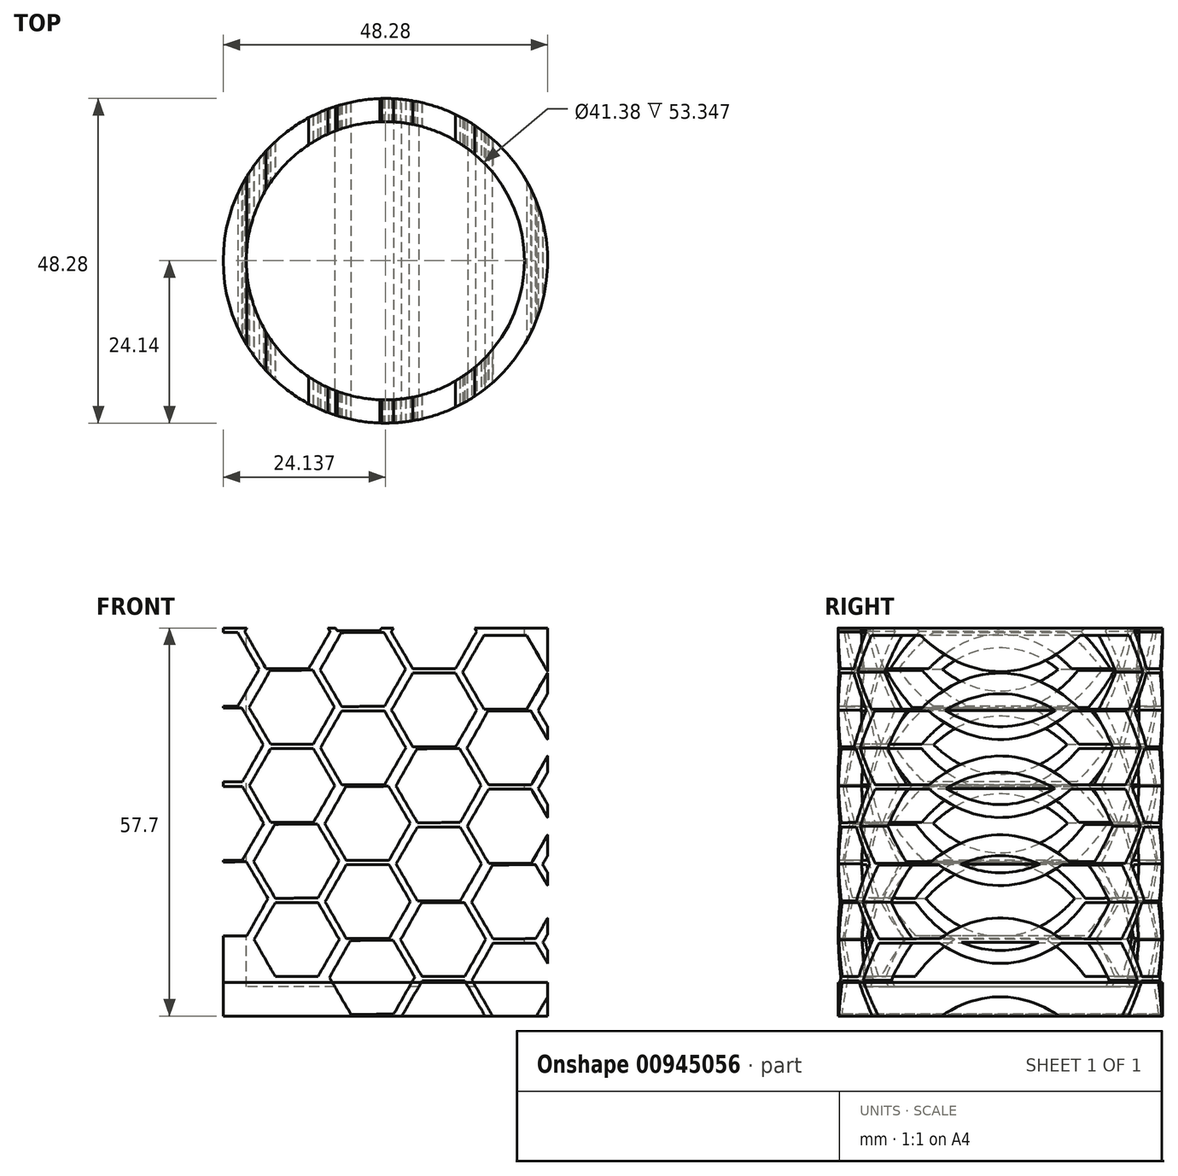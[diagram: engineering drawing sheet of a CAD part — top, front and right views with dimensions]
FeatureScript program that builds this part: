
annotation { "Feature Type Name" : "Feature", "Feature Type Description" : "" }
export const myFeature = defineFeature(function(context is Context, id is Id, definition is map)
    precondition{}
    {
        {
            var Q0;
            Q0=qCreatedBy(makeId("Front.planeOp"),FACE);
            var sketch = newSketch(context, id + "F0", { "sketchPlane" : qUnion([Q0])});
            skLineSegment(sketch, "E0", {"start": v(-46.54, 38.92) * mm, "end": v(-43.1, 38.92) * mm});
            skLineSegment(sketch, "E1", {"start": v(-46.54, 38.92) * mm, "end": v(-46.54, -18.78) * mm});
            skLineSegment(sketch, "E2", {"start": v(-43.1, 38.92) * mm, "end": v(-43.1, -14.43) * mm});
            skLineSegment(sketch, "E3", {"start": v(-43.1, -14.43) * mm, "end": v(-22.4, -14.43) * mm});
            skLineSegment(sketch, "E4", {"start": v(-22.4, -14.43) * mm, "end": v(-22.4, -18.78) * mm});
            skLineSegment(sketch, "E5", {"start": v(-22.4, -18.78) * mm, "end": v(-46.54, -18.78) * mm});
            skSolve(sketch);
        }
        {
            var Q0;
            Q0 = qSketchRegion(id + "F0", true);
            var Q1;
            Q1=sQuery(id+"F0.wireOp",EDGE,"E4");
            revolve(context, id + "F1", {"surfaceOperationType" : NewSurfaceOperationType.NEW, "entities" : qUnion([Q0]), "axis" : qUnion([Q1]), "revolveType" : RevolveType.FULL});
        }
        {
            var Q0;
            Q0=makeQuery(id+"F1.opRevolve","SWEPT_BODY",BODY,{"disambiguationData":[OSD([sQuery(id+"F0.wireOp",EDGE,"E0"),sQuery(id+"F0.wireOp",EDGE,"E1"),sQuery(id+"F0.wireOp",EDGE,"E2"),sQuery(id+"F0.wireOp",EDGE,"E3"),sQuery(id+"F0.wireOp",EDGE,"E4"),sQuery(id+"F0.wireOp",EDGE,"E5")])]});
            var Q1;
            Q1=qCreatedBy(makeId("Origin.pointOp"),VERTEX);
            transform(context, id + "F2", {"entities" : qUnion([Q0]), "transformType" : TransformType.TRANSLATION_3D, "dx" : 1 * mm, "dy" : 91.3 * mm, "dz" : -0.8 * mm, "makeCopy" : false});
        }
        {
            var Q0;
            Q0=qCreatedBy(makeId("Front.planeOp"),FACE);
            var sketch = newSketch(context, id + "F3", { "sketchPlane" : qUnion([Q0])});
            skCircle(sketch, "E6.cCircle", {"center": v(-88.91, 21.16) * mm, "radius": 5.5 * mm, "construction": true});
            skLineSegment(sketch, "E6.0", {"start": v(-82.56, 21.2) * mm, "end": v(-85.7, 15.69) * mm});
            skLineSegment(sketch, "E6.1", {"start": v(-85.7, 15.69) * mm, "end": v(-92.05, 15.64) * mm});
            skLineSegment(sketch, "E6.2", {"start": v(-92.05, 15.64) * mm, "end": v(-95.26, 21.12) * mm});
            skLineSegment(sketch, "E6.3", {"start": v(-95.26, 21.12) * mm, "end": v(-92.12, 26.64) * mm});
            skLineSegment(sketch, "E6.4", {"start": v(-92.12, 26.64) * mm, "end": v(-85.77, 26.69) * mm});
            skLineSegment(sketch, "E6.5", {"start": v(-85.77, 26.69) * mm, "end": v(-82.56, 21.2) * mm});
            skPoint(sketch, "E6.0.midPoint", {"position": v(-84.13, 18.45) * mm});
            skCircle(sketch, "E7.cCircle", {"center": v(-78.3, 15.13) * mm, "radius": 5.5 * mm, "construction": true});
            skLineSegment(sketch, "E7.0", {"start": v(-81.47, 9.63) * mm, "end": v(-84.65, 15.13) * mm});
            skLineSegment(sketch, "E7.1", {"start": v(-84.65, 15.13) * mm, "end": v(-81.47, 20.63) * mm});
            skLineSegment(sketch, "E7.2", {"start": v(-81.47, 20.63) * mm, "end": v(-75.12, 20.63) * mm});
            skLineSegment(sketch, "E7.3", {"start": v(-75.12, 20.63) * mm, "end": v(-71.94, 15.13) * mm});
            skLineSegment(sketch, "E7.4", {"start": v(-71.94, 15.13) * mm, "end": v(-75.12, 9.63) * mm});
            skLineSegment(sketch, "E7.5", {"start": v(-75.12, 9.63) * mm, "end": v(-81.47, 9.63) * mm});
            skPoint(sketch, "E7.0.midPoint", {"position": v(-83.06, 12.38) * mm});
            skLineSegment(sketch, "E8", {"start": v(-88.91, 21.16) * mm, "end": v(-78.3, 15.13) * mm});
            skLineSegment(sketch, "E9.1.0.0", {"start": v(-78.33, 26.78) * mm, "end": v(-67.72, 20.75) * mm});
            skLineSegment(sketch, "E9.1.0.1", {"start": v(-75.2, 32.3) * mm, "end": v(-71.98, 26.82) * mm});
            skPoint(sketch, "E9.1.0.2", {"position": v(-72.48, 18) * mm});
            skLineSegment(sketch, "E9.1.0.3", {"start": v(-81.47, 21.26) * mm, "end": v(-84.68, 26.74) * mm});
            skCircle(sketch, "E9.1.0.4", {"center": v(-67.72, 20.75) * mm, "radius": 5.5 * mm, "construction": true});
            skPoint(sketch, "E9.1.0.5", {"position": v(-73.55, 24.06) * mm});
            skCircle(sketch, "E9.1.0.6", {"center": v(-78.33, 26.78) * mm, "radius": 5.5 * mm, "construction": true});
            skLineSegment(sketch, "E9.1.0.7", {"start": v(-64.54, 15.25) * mm, "end": v(-70.9, 15.25) * mm});
            skLineSegment(sketch, "E9.1.0.8", {"start": v(-70.9, 15.25) * mm, "end": v(-74.07, 20.75) * mm});
            skLineSegment(sketch, "E9.1.0.9", {"start": v(-84.68, 26.74) * mm, "end": v(-81.55, 32.26) * mm});
            skLineSegment(sketch, "E9.1.0.10", {"start": v(-70.9, 26.25) * mm, "end": v(-64.54, 26.25) * mm});
            skLineSegment(sketch, "E9.1.0.11", {"start": v(-71.98, 26.82) * mm, "end": v(-75.12, 21.3) * mm});
            skLineSegment(sketch, "E9.1.0.12", {"start": v(-74.07, 20.75) * mm, "end": v(-70.9, 26.25) * mm});
            skLineSegment(sketch, "E9.1.0.13", {"start": v(-64.54, 26.25) * mm, "end": v(-61.37, 20.75) * mm});
            skLineSegment(sketch, "E9.1.0.14", {"start": v(-75.12, 21.3) * mm, "end": v(-81.47, 21.26) * mm});
            skLineSegment(sketch, "E9.1.0.15", {"start": v(-61.37, 20.75) * mm, "end": v(-64.54, 15.25) * mm});
            skLineSegment(sketch, "E9.1.0.16", {"start": v(-81.55, 32.26) * mm, "end": v(-75.2, 32.3) * mm});
            skLineSegment(sketch, "E9.2.0.0", {"start": v(-67.76, 32.4) * mm, "end": v(-57.14, 26.36) * mm});
            skLineSegment(sketch, "E9.2.0.1", {"start": v(-64.62, 37.92) * mm, "end": v(-61.4, 32.44) * mm});
            skPoint(sketch, "E9.2.0.2", {"position": v(-61.9, 23.61) * mm});
            skLineSegment(sketch, "E9.2.0.3", {"start": v(-70.9, 26.88) * mm, "end": v(-74.1, 32.35) * mm});
            skCircle(sketch, "E9.2.0.4", {"center": v(-57.14, 26.36) * mm, "radius": 5.5 * mm, "construction": true});
            skPoint(sketch, "E9.2.0.5", {"position": v(-62.97, 29.68) * mm});
            skCircle(sketch, "E9.2.0.6", {"center": v(-67.76, 32.4) * mm, "radius": 5.5 * mm, "construction": true});
            skLineSegment(sketch, "E9.2.0.7", {"start": v(-53.96, 20.86) * mm, "end": v(-60.31, 20.86) * mm});
            skLineSegment(sketch, "E9.2.0.8", {"start": v(-60.31, 20.86) * mm, "end": v(-63.5, 26.36) * mm});
            skLineSegment(sketch, "E9.2.0.9", {"start": v(-74.1, 32.35) * mm, "end": v(-70.97, 37.88) * mm});
            skLineSegment(sketch, "E9.2.0.10", {"start": v(-60.32, 31.86) * mm, "end": v(-53.96, 31.86) * mm});
            skLineSegment(sketch, "E9.2.0.11", {"start": v(-61.4, 32.44) * mm, "end": v(-64.54, 26.92) * mm});
            skLineSegment(sketch, "E9.2.0.12", {"start": v(-63.5, 26.36) * mm, "end": v(-60.32, 31.86) * mm});
            skLineSegment(sketch, "E9.2.0.13", {"start": v(-53.96, 31.86) * mm, "end": v(-50.79, 26.36) * mm});
            skLineSegment(sketch, "E9.2.0.14", {"start": v(-64.54, 26.92) * mm, "end": v(-70.9, 26.88) * mm});
            skLineSegment(sketch, "E9.2.0.15", {"start": v(-50.79, 26.36) * mm, "end": v(-53.96, 20.86) * mm});
            skLineSegment(sketch, "E9.2.0.16", {"start": v(-70.97, 37.88) * mm, "end": v(-64.62, 37.92) * mm});
            skLineSegment(sketch, "E9.3.0.0", {"start": v(-57.18, 38.01) * mm, "end": v(-46.56, 31.98) * mm});
            skLineSegment(sketch, "E9.3.0.1", {"start": v(-54.04, 43.54) * mm, "end": v(-50.83, 38.06) * mm});
            skPoint(sketch, "E9.3.0.2", {"position": v(-51.32, 29.23) * mm});
            skLineSegment(sketch, "E9.3.0.3", {"start": v(-60.32, 32.5) * mm, "end": v(-63.53, 37.97) * mm});
            skCircle(sketch, "E9.3.0.4", {"center": v(-46.56, 31.98) * mm, "radius": 5.5 * mm, "construction": true});
            skPoint(sketch, "E9.3.0.5", {"position": v(-52.4, 35.3) * mm});
            skCircle(sketch, "E9.3.0.6", {"center": v(-57.18, 38.01) * mm, "radius": 5.5 * mm, "construction": true});
            skLineSegment(sketch, "E9.3.0.7", {"start": v(-43.38, 26.48) * mm, "end": v(-49.74, 26.48) * mm});
            skLineSegment(sketch, "E9.3.0.8", {"start": v(-49.74, 26.48) * mm, "end": v(-52.91, 31.98) * mm});
            skLineSegment(sketch, "E9.3.0.9", {"start": v(-63.53, 37.97) * mm, "end": v(-60.4, 43.5) * mm});
            skLineSegment(sketch, "E9.3.0.10", {"start": v(-49.74, 37.48) * mm, "end": v(-43.39, 37.48) * mm});
            skLineSegment(sketch, "E9.3.0.11", {"start": v(-50.83, 38.06) * mm, "end": v(-53.97, 32.54) * mm});
            skLineSegment(sketch, "E9.3.0.12", {"start": v(-52.91, 31.98) * mm, "end": v(-49.74, 37.48) * mm});
            skLineSegment(sketch, "E9.3.0.13", {"start": v(-43.39, 37.48) * mm, "end": v(-40.21, 31.98) * mm});
            skLineSegment(sketch, "E9.3.0.14", {"start": v(-53.97, 32.54) * mm, "end": v(-60.32, 32.5) * mm});
            skLineSegment(sketch, "E9.3.0.15", {"start": v(-40.21, 31.98) * mm, "end": v(-43.38, 26.48) * mm});
            skLineSegment(sketch, "E9.3.0.16", {"start": v(-60.4, 43.5) * mm, "end": v(-54.04, 43.54) * mm});
            skLineSegment(sketch, "E9.4.0.0", {"start": v(-46.6, 43.63) * mm, "end": v(-35.98, 37.6) * mm});
            skLineSegment(sketch, "E9.4.0.1", {"start": v(-43.46, 49.15) * mm, "end": v(-40.25, 43.67) * mm});
            skPoint(sketch, "E9.4.0.2", {"position": v(-40.75, 34.85) * mm});
            skLineSegment(sketch, "E9.4.0.3", {"start": v(-49.74, 38.1) * mm, "end": v(-52.95, 43.59) * mm});
            skCircle(sketch, "E9.4.0.4", {"center": v(-35.98, 37.6) * mm, "radius": 5.5 * mm, "construction": true});
            skPoint(sketch, "E9.4.0.5", {"position": v(-41.82, 40.91) * mm});
            skCircle(sketch, "E9.4.0.6", {"center": v(-46.6, 43.63) * mm, "radius": 5.5 * mm, "construction": true});
            skLineSegment(sketch, "E9.4.0.7", {"start": v(-32.8, 32.1) * mm, "end": v(-39.16, 32.1) * mm});
            skLineSegment(sketch, "E9.4.0.8", {"start": v(-39.16, 32.1) * mm, "end": v(-42.33, 37.6) * mm});
            skLineSegment(sketch, "E9.4.0.9", {"start": v(-52.95, 43.59) * mm, "end": v(-49.81, 49.1) * mm});
            skLineSegment(sketch, "E9.4.0.10", {"start": v(-39.16, 43.1) * mm, "end": v(-32.8, 43.1) * mm});
            skLineSegment(sketch, "E9.4.0.11", {"start": v(-40.25, 43.67) * mm, "end": v(-43.39, 38.15) * mm});
            skLineSegment(sketch, "E9.4.0.12", {"start": v(-42.33, 37.6) * mm, "end": v(-39.16, 43.1) * mm});
            skLineSegment(sketch, "E9.4.0.13", {"start": v(-32.8, 43.1) * mm, "end": v(-29.63, 37.6) * mm});
            skLineSegment(sketch, "E9.4.0.14", {"start": v(-43.39, 38.15) * mm, "end": v(-49.74, 38.1) * mm});
            skLineSegment(sketch, "E9.4.0.15", {"start": v(-29.63, 37.6) * mm, "end": v(-32.8, 32.1) * mm});
            skLineSegment(sketch, "E9.4.0.16", {"start": v(-49.81, 49.1) * mm, "end": v(-43.46, 49.15) * mm});
            skLineSegment(sketch, "E9.5.0.0", {"start": v(-36.02, 49.25) * mm, "end": v(-25.4, 43.21) * mm});
            skLineSegment(sketch, "E9.5.0.1", {"start": v(-32.88, 54.77) * mm, "end": v(-29.67, 49.3) * mm});
            skPoint(sketch, "E9.5.0.2", {"position": v(-30.17, 40.46) * mm});
            skLineSegment(sketch, "E9.5.0.3", {"start": v(-39.16, 43.73) * mm, "end": v(-42.37, 49.2) * mm});
            skCircle(sketch, "E9.5.0.4", {"center": v(-25.4, 43.21) * mm, "radius": 5.5 * mm, "construction": true});
            skPoint(sketch, "E9.5.0.5", {"position": v(-31.24, 46.53) * mm});
            skCircle(sketch, "E9.5.0.6", {"center": v(-36.02, 49.25) * mm, "radius": 5.5 * mm, "construction": true});
            skLineSegment(sketch, "E9.5.0.7", {"start": v(-22.23, 37.71) * mm, "end": v(-28.58, 37.71) * mm});
            skLineSegment(sketch, "E9.5.0.8", {"start": v(-28.58, 37.71) * mm, "end": v(-31.76, 43.21) * mm});
            skLineSegment(sketch, "E9.5.0.9", {"start": v(-42.37, 49.2) * mm, "end": v(-39.23, 54.73) * mm});
            skLineSegment(sketch, "E9.5.0.10", {"start": v(-28.58, 48.71) * mm, "end": v(-22.23, 48.71) * mm});
            skLineSegment(sketch, "E9.5.0.11", {"start": v(-29.67, 49.3) * mm, "end": v(-32.8, 43.77) * mm});
            skLineSegment(sketch, "E9.5.0.12", {"start": v(-31.76, 43.21) * mm, "end": v(-28.58, 48.71) * mm});
            skLineSegment(sketch, "E9.5.0.13", {"start": v(-22.23, 48.71) * mm, "end": v(-19.05, 43.21) * mm});
            skLineSegment(sketch, "E9.5.0.14", {"start": v(-32.8, 43.77) * mm, "end": v(-39.16, 43.73) * mm});
            skLineSegment(sketch, "E9.5.0.15", {"start": v(-19.05, 43.21) * mm, "end": v(-22.23, 37.71) * mm});
            skLineSegment(sketch, "E9.5.0.16", {"start": v(-39.23, 54.73) * mm, "end": v(-32.88, 54.77) * mm});
            skLineSegment(sketch, "E9.direction1", {"start": v(-92.05, 15.64) * mm, "end": v(-81.47, 21.26) * mm, "construction": true});
            skLineSegment(sketch, "E10.1.0.0", {"start": v(-70.2, 3.98) * mm, "end": v(-59.63, 9.6) * mm, "construction": true});
            skPoint(sketch, "E10.1.0.1", {"position": v(-19.97, 29.25) * mm});
            skPoint(sketch, "E10.1.0.2", {"position": v(-41.13, 18.02) * mm});
            skLineSegment(sketch, "E10.1.0.3", {"start": v(-53.35, 20.64) * mm, "end": v(-50.14, 15.16) * mm});
            skCircle(sketch, "E10.1.0.4", {"center": v(-24.72, 20.32) * mm, "radius": 5.5 * mm, "construction": true});
            skPoint(sketch, "E10.1.0.5", {"position": v(-30.55, 23.63) * mm});
            skLineSegment(sketch, "E10.1.0.6", {"start": v(-38.55, 31.83) * mm, "end": v(-32.2, 31.87) * mm});
            skLineSegment(sketch, "E10.1.0.7", {"start": v(-24.76, 31.97) * mm, "end": v(-14.14, 25.93) * mm});
            skLineSegment(sketch, "E10.1.0.8", {"start": v(-14.18, 37.59) * mm, "end": v(-3.56, 31.55) * mm});
            skLineSegment(sketch, "E10.1.0.9", {"start": v(-67.07, 9.5) * mm, "end": v(-56.45, 3.47) * mm});
            skCircle(sketch, "E10.1.0.10", {"center": v(-56.45, 3.47) * mm, "radius": 5.5 * mm, "construction": true});
            skCircle(sketch, "E10.1.0.11", {"center": v(-24.76, 31.97) * mm, "radius": 5.5 * mm, "construction": true});
            skLineSegment(sketch, "E10.1.0.12", {"start": v(-27.9, 26.45) * mm, "end": v(-31.1, 31.93) * mm});
            skPoint(sketch, "E10.1.0.13", {"position": v(-51.7, 12.4) * mm});
            skCircle(sketch, "E10.1.0.14", {"center": v(-3.56, 31.55) * mm, "radius": 5.5 * mm, "construction": true});
            skLineSegment(sketch, "E10.1.0.15", {"start": v(-45.91, 20.74) * mm, "end": v(-35.3, 14.7) * mm});
            skPoint(sketch, "E10.1.0.16", {"position": v(-61.21, 0.72) * mm});
            skPoint(sketch, "E10.1.0.17", {"position": v(-29.48, 17.57) * mm});
            skCircle(sketch, "E10.1.0.18", {"center": v(-14.18, 37.59) * mm, "radius": 5.5 * mm, "construction": true});
            skPoint(sketch, "E10.1.0.19", {"position": v(-62.29, 6.78) * mm});
            skCircle(sketch, "E10.1.0.20", {"center": v(-35.33, 26.35) * mm, "radius": 5.5 * mm, "construction": true});
            skCircle(sketch, "E10.1.0.21", {"center": v(-45.87, 9.08) * mm, "radius": 5.5 * mm, "construction": true});
            skLineSegment(sketch, "E10.1.0.22", {"start": v(-35.33, 26.35) * mm, "end": v(-24.72, 20.32) * mm});
            skCircle(sketch, "E10.1.0.23", {"center": v(-14.14, 25.93) * mm, "radius": 5.5 * mm, "construction": true});
            skCircle(sketch, "E10.1.0.24", {"center": v(-35.3, 14.7) * mm, "radius": 5.5 * mm, "construction": true});
            skPoint(sketch, "E10.1.0.25", {"position": v(-40.06, 11.95) * mm});
            skPoint(sketch, "E10.1.0.26", {"position": v(-8.32, 28.8) * mm});
            skPoint(sketch, "E10.1.0.27", {"position": v(-50.64, 6.33) * mm});
            skLineSegment(sketch, "E10.1.0.28", {"start": v(-21.62, 37.49) * mm, "end": v(-18.4, 32.01) * mm});
            skCircle(sketch, "E10.1.0.29", {"center": v(-45.91, 20.74) * mm, "radius": 5.5 * mm, "construction": true});
            skPoint(sketch, "E10.1.0.30", {"position": v(-9.4, 34.87) * mm});
            skCircle(sketch, "E10.1.0.31", {"center": v(-56.5, 15.12) * mm, "radius": 5.5 * mm, "construction": true});
            skCircle(sketch, "E10.1.0.32", {"center": v(-67.07, 9.5) * mm, "radius": 5.5 * mm, "construction": true});
            skPoint(sketch, "E10.1.0.33", {"position": v(-18.9, 23.18) * mm});
            skLineSegment(sketch, "E10.1.0.34", {"start": v(-56.5, 15.12) * mm, "end": v(-45.87, 9.08) * mm});
            skLineSegment(sketch, "E10.1.0.35", {"start": v(-10.97, 31.44) * mm, "end": v(-7.79, 25.94) * mm});
            skLineSegment(sketch, "E10.1.0.36", {"start": v(-32.12, 20.2) * mm, "end": v(-28.94, 14.7) * mm});
            skLineSegment(sketch, "E10.1.0.37", {"start": v(-49.05, 14.58) * mm, "end": v(-42.7, 14.59) * mm});
            skLineSegment(sketch, "E10.1.0.38", {"start": v(-0.39, 26.05) * mm, "end": v(-6.74, 26.05) * mm});
            skLineSegment(sketch, "E10.1.0.39", {"start": v(-42.7, 3.59) * mm, "end": v(-49.05, 3.58) * mm});
            skLineSegment(sketch, "E10.1.0.40", {"start": v(-28.98, 26.4) * mm, "end": v(-32.12, 20.87) * mm});
            skLineSegment(sketch, "E10.1.0.41", {"start": v(-17.4, 43.06) * mm, "end": v(-11.04, 43.1) * mm});
            skLineSegment(sketch, "E10.1.0.42", {"start": v(-42.7, 15.26) * mm, "end": v(-49.05, 15.21) * mm});
            skLineSegment(sketch, "E10.1.0.43", {"start": v(-20.53, 37.54) * mm, "end": v(-17.4, 43.06) * mm});
            skLineSegment(sketch, "E10.1.0.44", {"start": v(-52.22, 9.08) * mm, "end": v(-49.05, 14.58) * mm});
            skLineSegment(sketch, "E10.1.0.45", {"start": v(-50.14, 15.16) * mm, "end": v(-53.28, 9.64) * mm});
            skLineSegment(sketch, "E10.1.0.46", {"start": v(-50.1, 3.47) * mm, "end": v(-53.28, -2.03) * mm});
            skLineSegment(sketch, "E10.1.0.47", {"start": v(-7.79, 25.94) * mm, "end": v(-10.96, 20.44) * mm});
            skLineSegment(sketch, "E10.1.0.48", {"start": v(-6.74, 26.05) * mm, "end": v(-9.91, 31.55) * mm});
            skLineSegment(sketch, "E10.1.0.49", {"start": v(-32.12, 9.2) * mm, "end": v(-38.47, 9.2) * mm});
            skLineSegment(sketch, "E10.1.0.50", {"start": v(-42.7, 14.59) * mm, "end": v(-39.52, 9.09) * mm});
            skLineSegment(sketch, "E10.1.0.51", {"start": v(-32.12, 20.87) * mm, "end": v(-38.47, 20.83) * mm});
            skLineSegment(sketch, "E10.1.0.52", {"start": v(-53.28, 9.64) * mm, "end": v(-59.63, 9.6) * mm});
            skLineSegment(sketch, "E10.1.0.53", {"start": v(-60.72, 9.55) * mm, "end": v(-63.86, 4.02) * mm});
            skLineSegment(sketch, "E10.1.0.54", {"start": v(-0.39, 37.05) * mm, "end": v(2.79, 31.55) * mm});
            skLineSegment(sketch, "E10.1.0.55", {"start": v(-20.5, 25.93) * mm, "end": v(-17.32, 31.43) * mm});
            skLineSegment(sketch, "E10.1.0.56", {"start": v(-27.9, 25.82) * mm, "end": v(-21.54, 25.82) * mm});
            skLineSegment(sketch, "E10.1.0.57", {"start": v(-38.47, 9.2) * mm, "end": v(-41.65, 14.7) * mm});
            skLineSegment(sketch, "E10.1.0.58", {"start": v(-17.31, 20.43) * mm, "end": v(-20.5, 25.93) * mm});
            skLineSegment(sketch, "E10.1.0.59", {"start": v(-38.47, 20.83) * mm, "end": v(-41.68, 26.3) * mm});
            skLineSegment(sketch, "E10.1.0.60", {"start": v(-41.65, 14.7) * mm, "end": v(-38.47, 20.2) * mm});
            skLineSegment(sketch, "E10.1.0.61", {"start": v(-59.63, 8.97) * mm, "end": v(-53.28, 8.97) * mm});
            skLineSegment(sketch, "E10.1.0.62", {"start": v(-18.37, 20.32) * mm, "end": v(-21.54, 14.82) * mm});
            skLineSegment(sketch, "E10.1.0.63", {"start": v(-49.12, 26.21) * mm, "end": v(-42.77, 26.26) * mm});
            skLineSegment(sketch, "E10.1.0.64", {"start": v(-31.1, 31.93) * mm, "end": v(-27.97, 37.45) * mm});
            skLineSegment(sketch, "E10.1.0.65", {"start": v(-9.91, 31.55) * mm, "end": v(-6.74, 37.05) * mm});
            skLineSegment(sketch, "E10.1.0.66", {"start": v(-62.8, 3.47) * mm, "end": v(-59.63, 8.97) * mm});
            skLineSegment(sketch, "E10.1.0.67", {"start": v(-11.04, 43.1) * mm, "end": v(-7.83, 37.63) * mm});
            skLineSegment(sketch, "E10.1.0.68", {"start": v(-52.26, 20.7) * mm, "end": v(-49.12, 26.21) * mm});
            skLineSegment(sketch, "E10.1.0.69", {"start": v(-59.63, 9.6) * mm, "end": v(-62.84, 15.08) * mm});
            skLineSegment(sketch, "E10.1.0.70", {"start": v(-32.2, 31.87) * mm, "end": v(-28.98, 26.4) * mm});
            skLineSegment(sketch, "E10.1.0.71", {"start": v(-39.52, 9.09) * mm, "end": v(-42.7, 3.59) * mm});
            skLineSegment(sketch, "E10.1.0.72", {"start": v(-59.63, -2.03) * mm, "end": v(-62.8, 3.47) * mm});
            skLineSegment(sketch, "E10.1.0.73", {"start": v(-31.07, 20.32) * mm, "end": v(-27.9, 25.82) * mm});
            skLineSegment(sketch, "E10.1.0.74", {"start": v(-17.32, 31.43) * mm, "end": v(-10.97, 31.44) * mm});
            skLineSegment(sketch, "E10.1.0.75", {"start": v(-21.54, 26.5) * mm, "end": v(-27.9, 26.45) * mm});
            skLineSegment(sketch, "E10.1.0.76", {"start": v(-59.7, 20.6) * mm, "end": v(-53.35, 20.64) * mm});
            skLineSegment(sketch, "E10.1.0.77", {"start": v(-62.84, 15.08) * mm, "end": v(-59.7, 20.6) * mm});
            skLineSegment(sketch, "E10.1.0.78", {"start": v(-27.97, 37.45) * mm, "end": v(-21.62, 37.49) * mm});
            skLineSegment(sketch, "E10.1.0.79", {"start": v(-39.56, 20.78) * mm, "end": v(-42.7, 15.26) * mm});
            skLineSegment(sketch, "E10.1.0.80", {"start": v(-73.42, 9.46) * mm, "end": v(-70.28, 14.98) * mm});
            skLineSegment(sketch, "E10.1.0.81", {"start": v(-17.32, 32.06) * mm, "end": v(-20.53, 37.54) * mm});
            skLineSegment(sketch, "E10.1.0.82", {"start": v(-63.93, 15.02) * mm, "end": v(-60.72, 9.55) * mm});
            skLineSegment(sketch, "E10.1.0.83", {"start": v(-42.77, 26.26) * mm, "end": v(-39.56, 20.78) * mm});
            skLineSegment(sketch, "E10.1.0.84", {"start": v(-38.47, 20.2) * mm, "end": v(-32.12, 20.2) * mm});
            skLineSegment(sketch, "E10.1.0.85", {"start": v(-41.68, 26.3) * mm, "end": v(-38.55, 31.83) * mm});
            skLineSegment(sketch, "E10.1.0.86", {"start": v(-21.54, 14.82) * mm, "end": v(-27.9, 14.82) * mm});
            skLineSegment(sketch, "E10.1.0.87", {"start": v(-27.9, 14.82) * mm, "end": v(-31.07, 20.32) * mm});
            skLineSegment(sketch, "E10.1.0.88", {"start": v(-10.96, 20.44) * mm, "end": v(-17.31, 20.43) * mm});
            skLineSegment(sketch, "E10.1.0.89", {"start": v(-28.94, 14.7) * mm, "end": v(-32.12, 9.2) * mm});
            skLineSegment(sketch, "E10.1.0.90", {"start": v(2.79, 31.55) * mm, "end": v(-0.39, 26.05) * mm});
            skLineSegment(sketch, "E10.1.0.91", {"start": v(-70.28, 14.98) * mm, "end": v(-63.93, 15.02) * mm});
            skLineSegment(sketch, "E10.1.0.92", {"start": v(-18.4, 32.01) * mm, "end": v(-21.54, 26.5) * mm});
            skLineSegment(sketch, "E10.1.0.93", {"start": v(-7.83, 37.63) * mm, "end": v(-10.97, 32.1) * mm});
            skLineSegment(sketch, "E10.1.0.94", {"start": v(-63.86, 4.02) * mm, "end": v(-70.2, 3.98) * mm});
            skLineSegment(sketch, "E10.1.0.95", {"start": v(-21.54, 25.82) * mm, "end": v(-18.37, 20.32) * mm});
            skLineSegment(sketch, "E10.1.0.96", {"start": v(-53.28, 8.97) * mm, "end": v(-50.1, 3.47) * mm});
            skLineSegment(sketch, "E10.1.0.97", {"start": v(-70.2, 3.98) * mm, "end": v(-73.42, 9.46) * mm});
            skLineSegment(sketch, "E10.1.0.98", {"start": v(-49.05, 15.21) * mm, "end": v(-52.26, 20.7) * mm});
            skLineSegment(sketch, "E10.1.0.99", {"start": v(-49.05, 3.58) * mm, "end": v(-52.22, 9.08) * mm});
            skLineSegment(sketch, "E10.1.0.100", {"start": v(-10.97, 32.1) * mm, "end": v(-17.32, 32.06) * mm});
            skLineSegment(sketch, "E10.1.0.101", {"start": v(-53.28, -2.03) * mm, "end": v(-59.63, -2.03) * mm});
            skLineSegment(sketch, "E10.1.0.102", {"start": v(-6.74, 37.05) * mm, "end": v(-0.39, 37.05) * mm});
            skLineSegment(sketch, "E10.2.0.0", {"start": v(-48.36, -7.68) * mm, "end": v(-37.78, -2.06) * mm, "construction": true});
            skPoint(sketch, "E10.2.0.1", {"position": v(1.87, 17.59) * mm});
            skPoint(sketch, "E10.2.0.2", {"position": v(-19.29, 6.36) * mm});
            skLineSegment(sketch, "E10.2.0.3", {"start": v(-31.5, 8.98) * mm, "end": v(-28.3, 3.5) * mm});
            skCircle(sketch, "E10.2.0.4", {"center": v(-2.87, 8.66) * mm, "radius": 5.5 * mm, "construction": true});
            skPoint(sketch, "E10.2.0.5", {"position": v(-8.7, 11.97) * mm});
            skLineSegment(sketch, "E10.2.0.6", {"start": v(-16.7, 20.17) * mm, "end": v(-10.35, 20.21) * mm});
            skLineSegment(sketch, "E10.2.0.7", {"start": v(-2.91, 20.3) * mm, "end": v(7.7, 14.27) * mm});
            skLineSegment(sketch, "E10.2.0.8", {"start": v(7.67, 25.92) * mm, "end": v(18.28, 19.89) * mm});
            skLineSegment(sketch, "E10.2.0.9", {"start": v(-45.22, -2.16) * mm, "end": v(-34.6, -8.2) * mm});
            skCircle(sketch, "E10.2.0.10", {"center": v(-34.6, -8.2) * mm, "radius": 5.5 * mm, "construction": true});
            skCircle(sketch, "E10.2.0.11", {"center": v(-2.91, 20.3) * mm, "radius": 5.5 * mm, "construction": true});
            skLineSegment(sketch, "E10.2.0.12", {"start": v(-6.05, 14.78) * mm, "end": v(-9.26, 20.26) * mm});
            skPoint(sketch, "E10.2.0.13", {"position": v(-29.87, 0.74) * mm});
            skCircle(sketch, "E10.2.0.14", {"center": v(18.28, 19.89) * mm, "radius": 5.5 * mm, "construction": true});
            skLineSegment(sketch, "E10.2.0.15", {"start": v(-24.07, 9.07) * mm, "end": v(-13.45, 3.04) * mm});
            skPoint(sketch, "E10.2.0.16", {"position": v(-39.37, -10.94) * mm});
            skPoint(sketch, "E10.2.0.17", {"position": v(-7.64, 5.9) * mm});
            skCircle(sketch, "E10.2.0.18", {"center": v(7.67, 25.92) * mm, "radius": 5.5 * mm, "construction": true});
            skPoint(sketch, "E10.2.0.19", {"position": v(-40.44, -4.88) * mm});
            skCircle(sketch, "E10.2.0.20", {"center": v(-13.5, 14.69) * mm, "radius": 5.5 * mm, "construction": true});
            skCircle(sketch, "E10.2.0.21", {"center": v(-24.03, -2.58) * mm, "radius": 5.5 * mm, "construction": true});
            skLineSegment(sketch, "E10.2.0.22", {"start": v(-13.5, 14.69) * mm, "end": v(-2.87, 8.66) * mm});
            skCircle(sketch, "E10.2.0.23", {"center": v(7.7, 14.27) * mm, "radius": 5.5 * mm, "construction": true});
            skCircle(sketch, "E10.2.0.24", {"center": v(-13.45, 3.04) * mm, "radius": 5.5 * mm, "construction": true});
            skPoint(sketch, "E10.2.0.25", {"position": v(-18.21, 0.29) * mm});
            skPoint(sketch, "E10.2.0.26", {"position": v(13.52, 17.14) * mm});
            skPoint(sketch, "E10.2.0.27", {"position": v(-28.8, -5.33) * mm});
            skLineSegment(sketch, "E10.2.0.28", {"start": v(0.23, 25.83) * mm, "end": v(3.44, 20.35) * mm});
            skCircle(sketch, "E10.2.0.29", {"center": v(-24.07, 9.07) * mm, "radius": 5.5 * mm, "construction": true});
            skPoint(sketch, "E10.2.0.30", {"position": v(12.45, 23.2) * mm});
            skCircle(sketch, "E10.2.0.31", {"center": v(-34.65, 3.46) * mm, "radius": 5.5 * mm, "construction": true});
            skCircle(sketch, "E10.2.0.32", {"center": v(-45.22, -2.16) * mm, "radius": 5.5 * mm, "construction": true});
            skPoint(sketch, "E10.2.0.33", {"position": v(2.94, 11.52) * mm});
            skLineSegment(sketch, "E10.2.0.34", {"start": v(-34.65, 3.46) * mm, "end": v(-24.03, -2.58) * mm});
            skLineSegment(sketch, "E10.2.0.35", {"start": v(10.88, 19.77) * mm, "end": v(14.05, 14.27) * mm});
            skLineSegment(sketch, "E10.2.0.36", {"start": v(-10.28, 8.54) * mm, "end": v(-7.1, 3.04) * mm});
            skLineSegment(sketch, "E10.2.0.37", {"start": v(-27.2, 2.92) * mm, "end": v(-20.86, 2.92) * mm});
            skLineSegment(sketch, "E10.2.0.38", {"start": v(21.46, 14.39) * mm, "end": v(15.1, 14.39) * mm});
            skLineSegment(sketch, "E10.2.0.39", {"start": v(-20.85, -8.08) * mm, "end": v(-27.2, -8.08) * mm});
            skLineSegment(sketch, "E10.2.0.40", {"start": v(-7.14, 14.73) * mm, "end": v(-10.28, 9.21) * mm});
            skLineSegment(sketch, "E10.2.0.41", {"start": v(4.45, 31.4) * mm, "end": v(10.8, 31.44) * mm});
            skLineSegment(sketch, "E10.2.0.42", {"start": v(-20.86, 3.6) * mm, "end": v(-27.2, 3.55) * mm});
            skLineSegment(sketch, "E10.2.0.43", {"start": v(1.31, 25.88) * mm, "end": v(4.45, 31.4) * mm});
            skLineSegment(sketch, "E10.2.0.44", {"start": v(-30.38, -2.58) * mm, "end": v(-27.2, 2.92) * mm});
            skLineSegment(sketch, "E10.2.0.45", {"start": v(-28.3, 3.5) * mm, "end": v(-31.43, -2.02) * mm});
            skLineSegment(sketch, "E10.2.0.46", {"start": v(-28.26, -8.2) * mm, "end": v(-31.43, -13.7) * mm});
            skLineSegment(sketch, "E10.2.0.47", {"start": v(14.05, 14.27) * mm, "end": v(10.88, 8.77) * mm});
            skLineSegment(sketch, "E10.2.0.48", {"start": v(15.1, 14.39) * mm, "end": v(11.93, 19.89) * mm});
            skLineSegment(sketch, "E10.2.0.49", {"start": v(-10.28, -2.46) * mm, "end": v(-16.63, -2.46) * mm});
            skLineSegment(sketch, "E10.2.0.50", {"start": v(-20.86, 2.92) * mm, "end": v(-17.68, -2.58) * mm});
            skLineSegment(sketch, "E10.2.0.51", {"start": v(-10.28, 9.21) * mm, "end": v(-16.63, 9.17) * mm});
            skLineSegment(sketch, "E10.2.0.52", {"start": v(-31.43, -2.02) * mm, "end": v(-37.78, -2.06) * mm});
            skLineSegment(sketch, "E10.2.0.53", {"start": v(-38.87, -2.12) * mm, "end": v(-42.01, -7.64) * mm});
            skLineSegment(sketch, "E10.2.0.54", {"start": v(21.46, 25.39) * mm, "end": v(24.63, 19.89) * mm});
            skLineSegment(sketch, "E10.2.0.55", {"start": v(1.35, 14.27) * mm, "end": v(4.53, 19.77) * mm});
            skLineSegment(sketch, "E10.2.0.56", {"start": v(-6.05, 14.16) * mm, "end": v(0.3, 14.16) * mm});
            skLineSegment(sketch, "E10.2.0.57", {"start": v(-16.63, -2.46) * mm, "end": v(-19.8, 3.04) * mm});
            skLineSegment(sketch, "E10.2.0.58", {"start": v(4.53, 8.77) * mm, "end": v(1.35, 14.27) * mm});
            skLineSegment(sketch, "E10.2.0.59", {"start": v(-16.63, 9.17) * mm, "end": v(-19.84, 14.65) * mm});
            skLineSegment(sketch, "E10.2.0.60", {"start": v(-19.8, 3.04) * mm, "end": v(-16.63, 8.54) * mm});
            skLineSegment(sketch, "E10.2.0.61", {"start": v(-37.78, -2.7) * mm, "end": v(-31.43, -2.7) * mm});
            skLineSegment(sketch, "E10.2.0.62", {"start": v(3.48, 8.66) * mm, "end": v(0.3, 3.16) * mm});
            skLineSegment(sketch, "E10.2.0.63", {"start": v(-27.28, 14.55) * mm, "end": v(-20.93, 14.6) * mm});
            skLineSegment(sketch, "E10.2.0.64", {"start": v(-9.26, 20.26) * mm, "end": v(-6.13, 25.78) * mm});
            skLineSegment(sketch, "E10.2.0.65", {"start": v(11.93, 19.89) * mm, "end": v(15.1, 25.39) * mm});
            skLineSegment(sketch, "E10.2.0.66", {"start": v(-40.96, -8.2) * mm, "end": v(-37.78, -2.7) * mm});
            skLineSegment(sketch, "E10.2.0.67", {"start": v(10.8, 31.44) * mm, "end": v(14.02, 25.97) * mm});
            skLineSegment(sketch, "E10.2.0.68", {"start": v(-30.42, 9.03) * mm, "end": v(-27.28, 14.55) * mm});
            skLineSegment(sketch, "E10.2.0.69", {"start": v(-37.78, -2.06) * mm, "end": v(-41, 3.41) * mm});
            skLineSegment(sketch, "E10.2.0.70", {"start": v(-10.35, 20.21) * mm, "end": v(-7.14, 14.73) * mm});
            skLineSegment(sketch, "E10.2.0.71", {"start": v(-17.68, -2.58) * mm, "end": v(-20.85, -8.08) * mm});
            skLineSegment(sketch, "E10.2.0.72", {"start": v(-37.78, -13.7) * mm, "end": v(-40.96, -8.2) * mm});
            skLineSegment(sketch, "E10.2.0.73", {"start": v(-9.23, 8.65) * mm, "end": v(-6.05, 14.16) * mm});
            skLineSegment(sketch, "E10.2.0.74", {"start": v(4.53, 19.77) * mm, "end": v(10.88, 19.77) * mm});
            skLineSegment(sketch, "E10.2.0.75", {"start": v(0.3, 14.83) * mm, "end": v(-6.05, 14.78) * mm});
            skLineSegment(sketch, "E10.2.0.76", {"start": v(-37.86, 8.93) * mm, "end": v(-31.5, 8.98) * mm});
            skLineSegment(sketch, "E10.2.0.77", {"start": v(-41, 3.41) * mm, "end": v(-37.86, 8.93) * mm});
            skLineSegment(sketch, "E10.2.0.78", {"start": v(-6.13, 25.78) * mm, "end": v(0.23, 25.83) * mm});
            skLineSegment(sketch, "E10.2.0.79", {"start": v(-17.72, 9.12) * mm, "end": v(-20.86, 3.6) * mm});
            skLineSegment(sketch, "E10.2.0.80", {"start": v(-51.58, -2.2) * mm, "end": v(-48.44, 3.32) * mm});
            skLineSegment(sketch, "E10.2.0.81", {"start": v(4.53, 20.4) * mm, "end": v(1.31, 25.88) * mm});
            skLineSegment(sketch, "E10.2.0.82", {"start": v(-42.09, 3.36) * mm, "end": v(-38.87, -2.12) * mm});
            skLineSegment(sketch, "E10.2.0.83", {"start": v(-20.93, 14.6) * mm, "end": v(-17.72, 9.12) * mm});
            skLineSegment(sketch, "E10.2.0.84", {"start": v(-16.63, 8.54) * mm, "end": v(-10.28, 8.54) * mm});
            skLineSegment(sketch, "E10.2.0.85", {"start": v(-19.84, 14.65) * mm, "end": v(-16.7, 20.17) * mm});
            skLineSegment(sketch, "E10.2.0.86", {"start": v(0.3, 3.16) * mm, "end": v(-6.05, 3.16) * mm});
            skLineSegment(sketch, "E10.2.0.87", {"start": v(-6.05, 3.16) * mm, "end": v(-9.23, 8.65) * mm});
            skLineSegment(sketch, "E10.2.0.88", {"start": v(10.88, 8.77) * mm, "end": v(4.53, 8.77) * mm});
            skLineSegment(sketch, "E10.2.0.89", {"start": v(-7.1, 3.04) * mm, "end": v(-10.28, -2.46) * mm});
            skLineSegment(sketch, "E10.2.0.90", {"start": v(24.63, 19.89) * mm, "end": v(21.46, 14.39) * mm});
            skLineSegment(sketch, "E10.2.0.91", {"start": v(-48.44, 3.32) * mm, "end": v(-42.09, 3.36) * mm});
            skLineSegment(sketch, "E10.2.0.92", {"start": v(3.44, 20.35) * mm, "end": v(0.3, 14.83) * mm});
            skLineSegment(sketch, "E10.2.0.93", {"start": v(14.02, 25.97) * mm, "end": v(10.88, 20.44) * mm});
            skLineSegment(sketch, "E10.2.0.94", {"start": v(-42.01, -7.64) * mm, "end": v(-48.36, -7.68) * mm});
            skLineSegment(sketch, "E10.2.0.95", {"start": v(0.3, 14.16) * mm, "end": v(3.48, 8.66) * mm});
            skLineSegment(sketch, "E10.2.0.96", {"start": v(-31.43, -2.7) * mm, "end": v(-28.26, -8.2) * mm});
            skLineSegment(sketch, "E10.2.0.97", {"start": v(-48.36, -7.68) * mm, "end": v(-51.58, -2.2) * mm});
            skLineSegment(sketch, "E10.2.0.98", {"start": v(-27.2, 3.55) * mm, "end": v(-30.42, 9.03) * mm});
            skLineSegment(sketch, "E10.2.0.99", {"start": v(-27.2, -8.08) * mm, "end": v(-30.38, -2.58) * mm});
            skLineSegment(sketch, "E10.2.0.100", {"start": v(10.88, 20.44) * mm, "end": v(4.53, 20.4) * mm});
            skLineSegment(sketch, "E10.2.0.101", {"start": v(-31.43, -13.7) * mm, "end": v(-37.78, -13.7) * mm});
            skLineSegment(sketch, "E10.2.0.102", {"start": v(15.1, 25.39) * mm, "end": v(21.46, 25.39) * mm});
            skLineSegment(sketch, "E10.3.0.0", {"start": v(-26.52, -19.34) * mm, "end": v(-15.94, -13.73) * mm, "construction": true});
            skPoint(sketch, "E10.3.0.1", {"position": v(23.71, 5.93) * mm});
            skPoint(sketch, "E10.3.0.2", {"position": v(2.56, -5.3) * mm});
            skLineSegment(sketch, "E10.3.0.3", {"start": v(-9.67, -2.68) * mm, "end": v(-6.45, -8.16) * mm});
            skCircle(sketch, "E10.3.0.4", {"center": v(18.97, -3) * mm, "radius": 5.5 * mm, "construction": true});
            skPoint(sketch, "E10.3.0.5", {"position": v(13.13, 0.3) * mm});
            skLineSegment(sketch, "E10.3.0.6", {"start": v(5.14, 8.5) * mm, "end": v(11.5, 8.55) * mm});
            skLineSegment(sketch, "E10.3.0.7", {"start": v(18.93, 8.64) * mm, "end": v(29.55, 2.6) * mm});
            skLineSegment(sketch, "E10.3.0.8", {"start": v(29.5, 14.26) * mm, "end": v(40.13, 8.23) * mm});
            skLineSegment(sketch, "E10.3.0.9", {"start": v(-23.38, -13.82) * mm, "end": v(-12.76, -19.86) * mm});
            skCircle(sketch, "E10.3.0.10", {"center": v(-12.76, -19.86) * mm, "radius": 5.5 * mm, "construction": true});
            skCircle(sketch, "E10.3.0.11", {"center": v(18.93, 8.64) * mm, "radius": 5.5 * mm, "construction": true});
            skLineSegment(sketch, "E10.3.0.12", {"start": v(15.8, 3.12) * mm, "end": v(12.58, 8.6) * mm});
            skPoint(sketch, "E10.3.0.13", {"position": v(-8.02, -10.92) * mm});
            skCircle(sketch, "E10.3.0.14", {"center": v(40.13, 8.23) * mm, "radius": 5.5 * mm, "construction": true});
            skLineSegment(sketch, "E10.3.0.15", {"start": v(-2.23, -2.59) * mm, "end": v(8.4, -8.62) * mm});
            skPoint(sketch, "E10.3.0.16", {"position": v(-17.53, -22.6) * mm});
            skPoint(sketch, "E10.3.0.17", {"position": v(14.2, -5.76) * mm});
            skCircle(sketch, "E10.3.0.18", {"center": v(29.5, 14.26) * mm, "radius": 5.5 * mm, "construction": true});
            skPoint(sketch, "E10.3.0.19", {"position": v(-18.6, -16.54) * mm});
            skCircle(sketch, "E10.3.0.20", {"center": v(8.35, 3.03) * mm, "radius": 5.5 * mm, "construction": true});
            skCircle(sketch, "E10.3.0.21", {"center": v(-2.19, -14.24) * mm, "radius": 5.5 * mm, "construction": true});
            skLineSegment(sketch, "E10.3.0.22", {"start": v(8.35, 3.03) * mm, "end": v(18.97, -3) * mm});
            skCircle(sketch, "E10.3.0.23", {"center": v(29.55, 2.6) * mm, "radius": 5.5 * mm, "construction": true});
            skCircle(sketch, "E10.3.0.24", {"center": v(8.4, -8.62) * mm, "radius": 5.5 * mm, "construction": true});
            skPoint(sketch, "E10.3.0.25", {"position": v(3.63, -11.37) * mm});
            skPoint(sketch, "E10.3.0.26", {"position": v(35.36, 5.48) * mm});
            skPoint(sketch, "E10.3.0.27", {"position": v(-6.95, -17) * mm});
            skLineSegment(sketch, "E10.3.0.28", {"start": v(22.07, 14.17) * mm, "end": v(25.28, 8.69) * mm});
            skCircle(sketch, "E10.3.0.29", {"center": v(-2.23, -2.59) * mm, "radius": 5.5 * mm, "construction": true});
            skPoint(sketch, "E10.3.0.30", {"position": v(34.3, 11.54) * mm});
            skCircle(sketch, "E10.3.0.31", {"center": v(-12.8, -8.2) * mm, "radius": 5.5 * mm, "construction": true});
            skCircle(sketch, "E10.3.0.32", {"center": v(-23.38, -13.82) * mm, "radius": 5.5 * mm, "construction": true});
            skPoint(sketch, "E10.3.0.33", {"position": v(24.78, -0.14) * mm});
            skLineSegment(sketch, "E10.3.0.34", {"start": v(-12.8, -8.2) * mm, "end": v(-2.19, -14.24) * mm});
            skLineSegment(sketch, "E10.3.0.35", {"start": v(32.72, 8.11) * mm, "end": v(35.9, 2.61) * mm});
            skLineSegment(sketch, "E10.3.0.36", {"start": v(11.57, -3.12) * mm, "end": v(14.74, -8.62) * mm});
            skLineSegment(sketch, "E10.3.0.37", {"start": v(-5.36, -8.74) * mm, "end": v(0.99, -8.74) * mm});
            skLineSegment(sketch, "E10.3.0.38", {"start": v(43.3, 2.73) * mm, "end": v(36.95, 2.73) * mm});
            skLineSegment(sketch, "E10.3.0.39", {"start": v(0.99, -19.74) * mm, "end": v(-5.36, -19.74) * mm});
            skLineSegment(sketch, "E10.3.0.40", {"start": v(14.7, 3.07) * mm, "end": v(11.57, -2.45) * mm});
            skLineSegment(sketch, "E10.3.0.41", {"start": v(26.3, 19.74) * mm, "end": v(32.65, 19.78) * mm});
            skLineSegment(sketch, "E10.3.0.42", {"start": v(0.99, -8.07) * mm, "end": v(-5.36, -8.11) * mm});
            skLineSegment(sketch, "E10.3.0.43", {"start": v(23.16, 14.22) * mm, "end": v(26.3, 19.74) * mm});
            skLineSegment(sketch, "E10.3.0.44", {"start": v(-8.54, -14.24) * mm, "end": v(-5.36, -8.74) * mm});
            skLineSegment(sketch, "E10.3.0.45", {"start": v(-6.45, -8.16) * mm, "end": v(-9.6, -13.68) * mm});
            skLineSegment(sketch, "E10.3.0.46", {"start": v(-6.41, -19.86) * mm, "end": v(-9.59, -25.36) * mm});
            skLineSegment(sketch, "E10.3.0.47", {"start": v(35.9, 2.61) * mm, "end": v(32.72, -2.89) * mm});
            skLineSegment(sketch, "E10.3.0.48", {"start": v(36.95, 2.73) * mm, "end": v(33.77, 8.23) * mm});
            skLineSegment(sketch, "E10.3.0.49", {"start": v(11.57, -14.12) * mm, "end": v(5.22, -14.12) * mm});
            skLineSegment(sketch, "E10.3.0.50", {"start": v(0.99, -8.74) * mm, "end": v(4.16, -14.24) * mm});
            skLineSegment(sketch, "E10.3.0.51", {"start": v(11.57, -2.45) * mm, "end": v(5.21, -2.5) * mm});
            skLineSegment(sketch, "E10.3.0.52", {"start": v(-9.6, -13.68) * mm, "end": v(-15.94, -13.73) * mm});
            skLineSegment(sketch, "E10.3.0.53", {"start": v(-17.03, -13.78) * mm, "end": v(-20.17, -19.3) * mm});
            skLineSegment(sketch, "E10.3.0.54", {"start": v(43.3, 13.73) * mm, "end": v(46.48, 8.23) * mm});
            skLineSegment(sketch, "E10.3.0.55", {"start": v(23.2, 2.6) * mm, "end": v(26.37, 8.1) * mm});
            skLineSegment(sketch, "E10.3.0.56", {"start": v(15.8, 2.5) * mm, "end": v(22.14, 2.5) * mm});
            skLineSegment(sketch, "E10.3.0.57", {"start": v(5.22, -14.12) * mm, "end": v(2.04, -8.62) * mm});
            skLineSegment(sketch, "E10.3.0.58", {"start": v(26.37, -2.9) * mm, "end": v(23.2, 2.6) * mm});
            skLineSegment(sketch, "E10.3.0.59", {"start": v(5.21, -2.5) * mm, "end": v(2, 2.98) * mm});
            skLineSegment(sketch, "E10.3.0.60", {"start": v(2.04, -8.62) * mm, "end": v(5.21, -3.12) * mm});
            skLineSegment(sketch, "E10.3.0.61", {"start": v(-15.94, -14.36) * mm, "end": v(-9.6, -14.36) * mm});
            skLineSegment(sketch, "E10.3.0.62", {"start": v(25.32, -3) * mm, "end": v(22.15, -8.5) * mm});
            skLineSegment(sketch, "E10.3.0.63", {"start": v(-5.44, 2.89) * mm, "end": v(0.91, 2.93) * mm});
            skLineSegment(sketch, "E10.3.0.64", {"start": v(12.58, 8.6) * mm, "end": v(15.72, 14.12) * mm});
            skLineSegment(sketch, "E10.3.0.65", {"start": v(33.77, 8.23) * mm, "end": v(36.95, 13.73) * mm});
            skLineSegment(sketch, "E10.3.0.66", {"start": v(-19.12, -19.86) * mm, "end": v(-15.94, -14.36) * mm});
            skLineSegment(sketch, "E10.3.0.67", {"start": v(32.65, 19.78) * mm, "end": v(35.86, 14.3) * mm});
            skLineSegment(sketch, "E10.3.0.68", {"start": v(-8.58, -2.63) * mm, "end": v(-5.44, 2.89) * mm});
            skLineSegment(sketch, "E10.3.0.69", {"start": v(-15.94, -13.73) * mm, "end": v(-19.15, -8.25) * mm});
            skLineSegment(sketch, "E10.3.0.70", {"start": v(11.5, 8.55) * mm, "end": v(14.7, 3.07) * mm});
            skLineSegment(sketch, "E10.3.0.71", {"start": v(4.16, -14.24) * mm, "end": v(0.99, -19.74) * mm});
            skLineSegment(sketch, "E10.3.0.72", {"start": v(-15.94, -25.36) * mm, "end": v(-19.12, -19.86) * mm});
            skLineSegment(sketch, "E10.3.0.73", {"start": v(12.62, -3) * mm, "end": v(15.8, 2.5) * mm});
            skLineSegment(sketch, "E10.3.0.74", {"start": v(26.37, 8.1) * mm, "end": v(32.72, 8.11) * mm});
            skLineSegment(sketch, "E10.3.0.75", {"start": v(22.14, 3.17) * mm, "end": v(15.8, 3.12) * mm});
            skLineSegment(sketch, "E10.3.0.76", {"start": v(-16.02, -2.73) * mm, "end": v(-9.67, -2.68) * mm});
            skLineSegment(sketch, "E10.3.0.77", {"start": v(-19.15, -8.25) * mm, "end": v(-16.02, -2.73) * mm});
            skLineSegment(sketch, "E10.3.0.78", {"start": v(15.72, 14.12) * mm, "end": v(22.07, 14.17) * mm});
            skLineSegment(sketch, "E10.3.0.79", {"start": v(4.13, -2.55) * mm, "end": v(0.99, -8.07) * mm});
            skLineSegment(sketch, "E10.3.0.80", {"start": v(-29.73, -13.87) * mm, "end": v(-26.6, -8.34) * mm});
            skLineSegment(sketch, "E10.3.0.81", {"start": v(26.37, 8.74) * mm, "end": v(23.16, 14.22) * mm});
            skLineSegment(sketch, "E10.3.0.82", {"start": v(-20.24, -8.3) * mm, "end": v(-17.03, -13.78) * mm});
            skLineSegment(sketch, "E10.3.0.83", {"start": v(0.91, 2.93) * mm, "end": v(4.13, -2.55) * mm});
            skLineSegment(sketch, "E10.3.0.84", {"start": v(5.21, -3.12) * mm, "end": v(11.57, -3.12) * mm});
            skLineSegment(sketch, "E10.3.0.85", {"start": v(2, 2.98) * mm, "end": v(5.14, 8.5) * mm});
            skLineSegment(sketch, "E10.3.0.86", {"start": v(22.15, -8.5) * mm, "end": v(15.8, -8.5) * mm});
            skLineSegment(sketch, "E10.3.0.87", {"start": v(15.8, -8.5) * mm, "end": v(12.62, -3) * mm});
            skLineSegment(sketch, "E10.3.0.88", {"start": v(32.72, -2.89) * mm, "end": v(26.37, -2.9) * mm});
            skLineSegment(sketch, "E10.3.0.89", {"start": v(14.74, -8.62) * mm, "end": v(11.57, -14.12) * mm});
            skLineSegment(sketch, "E10.3.0.90", {"start": v(46.48, 8.23) * mm, "end": v(43.3, 2.73) * mm});
            skLineSegment(sketch, "E10.3.0.91", {"start": v(-26.6, -8.34) * mm, "end": v(-20.24, -8.3) * mm});
            skLineSegment(sketch, "E10.3.0.92", {"start": v(25.28, 8.69) * mm, "end": v(22.14, 3.17) * mm});
            skLineSegment(sketch, "E10.3.0.93", {"start": v(35.86, 14.3) * mm, "end": v(32.72, 8.78) * mm});
            skLineSegment(sketch, "E10.3.0.94", {"start": v(-20.17, -19.3) * mm, "end": v(-26.52, -19.34) * mm});
            skLineSegment(sketch, "E10.3.0.95", {"start": v(22.14, 2.5) * mm, "end": v(25.32, -3) * mm});
            skLineSegment(sketch, "E10.3.0.96", {"start": v(-9.6, -14.36) * mm, "end": v(-6.41, -19.86) * mm});
            skLineSegment(sketch, "E10.3.0.97", {"start": v(-26.52, -19.34) * mm, "end": v(-29.73, -13.87) * mm});
            skLineSegment(sketch, "E10.3.0.98", {"start": v(-5.36, -8.11) * mm, "end": v(-8.58, -2.63) * mm});
            skLineSegment(sketch, "E10.3.0.99", {"start": v(-5.36, -19.74) * mm, "end": v(-8.54, -14.24) * mm});
            skLineSegment(sketch, "E10.3.0.100", {"start": v(32.72, 8.78) * mm, "end": v(26.37, 8.74) * mm});
            skLineSegment(sketch, "E10.3.0.101", {"start": v(-9.59, -25.36) * mm, "end": v(-15.94, -25.36) * mm});
            skLineSegment(sketch, "E10.3.0.102", {"start": v(36.95, 13.73) * mm, "end": v(43.3, 13.73) * mm});
            skLineSegment(sketch, "E10.4.0.0", {"start": v(-4.68, -31) * mm, "end": v(5.9, -25.39) * mm, "construction": true});
            skPoint(sketch, "E10.4.0.1", {"position": v(45.56, -5.74) * mm});
            skPoint(sketch, "E10.4.0.2", {"position": v(24.4, -16.97) * mm});
            skLineSegment(sketch, "E10.4.0.3", {"start": v(12.18, -14.35) * mm, "end": v(15.4, -19.83) * mm});
            skCircle(sketch, "E10.4.0.4", {"center": v(40.81, -14.67) * mm, "radius": 5.5 * mm, "construction": true});
            skPoint(sketch, "E10.4.0.5", {"position": v(34.98, -11.35) * mm});
            skLineSegment(sketch, "E10.4.0.6", {"start": v(26.98, -3.16) * mm, "end": v(33.33, -3.11) * mm});
            skLineSegment(sketch, "E10.4.0.7", {"start": v(40.77, -3.02) * mm, "end": v(51.4, -9.05) * mm});
            skLineSegment(sketch, "E10.4.0.8", {"start": v(51.35, 2.6) * mm, "end": v(61.97, -3.44) * mm});
            skLineSegment(sketch, "E10.4.0.9", {"start": v(-1.54, -25.48) * mm, "end": v(9.08, -31.52) * mm});
            skCircle(sketch, "E10.4.0.10", {"center": v(9.08, -31.52) * mm, "radius": 5.5 * mm, "construction": true});
            skCircle(sketch, "E10.4.0.11", {"center": v(40.77, -3.02) * mm, "radius": 5.5 * mm, "construction": true});
            skLineSegment(sketch, "E10.4.0.12", {"start": v(37.64, -8.54) * mm, "end": v(34.42, -3.06) * mm});
            skPoint(sketch, "E10.4.0.13", {"position": v(13.82, -22.59) * mm});
            skCircle(sketch, "E10.4.0.14", {"center": v(61.97, -3.44) * mm, "radius": 5.5 * mm, "construction": true});
            skLineSegment(sketch, "E10.4.0.15", {"start": v(19.62, -14.25) * mm, "end": v(30.23, -20.29) * mm});
            skPoint(sketch, "E10.4.0.16", {"position": v(4.32, -34.27) * mm});
            skPoint(sketch, "E10.4.0.17", {"position": v(36.05, -17.42) * mm});
            skCircle(sketch, "E10.4.0.18", {"center": v(51.35, 2.6) * mm, "radius": 5.5 * mm, "construction": true});
            skPoint(sketch, "E10.4.0.19", {"position": v(3.24, -28.2) * mm});
            skCircle(sketch, "E10.4.0.20", {"center": v(30.2, -8.64) * mm, "radius": 5.5 * mm, "construction": true});
            skCircle(sketch, "E10.4.0.21", {"center": v(19.66, -25.9) * mm, "radius": 5.5 * mm, "construction": true});
            skLineSegment(sketch, "E10.4.0.22", {"start": v(30.2, -8.64) * mm, "end": v(40.81, -14.67) * mm});
            skCircle(sketch, "E10.4.0.23", {"center": v(51.4, -9.05) * mm, "radius": 5.5 * mm, "construction": true});
            skCircle(sketch, "E10.4.0.24", {"center": v(30.23, -20.29) * mm, "radius": 5.5 * mm, "construction": true});
            skPoint(sketch, "E10.4.0.25", {"position": v(25.47, -23.04) * mm});
            skPoint(sketch, "E10.4.0.26", {"position": v(57.2, -6.19) * mm});
            skPoint(sketch, "E10.4.0.27", {"position": v(14.9, -28.65) * mm});
            skLineSegment(sketch, "E10.4.0.28", {"start": v(43.91, 2.5) * mm, "end": v(47.13, -2.98) * mm});
            skCircle(sketch, "E10.4.0.29", {"center": v(19.62, -14.25) * mm, "radius": 5.5 * mm, "construction": true});
            skPoint(sketch, "E10.4.0.30", {"position": v(56.13, -0.12) * mm});
            skCircle(sketch, "E10.4.0.31", {"center": v(9.04, -19.87) * mm, "radius": 5.5 * mm, "construction": true});
            skCircle(sketch, "E10.4.0.32", {"center": v(-1.54, -25.48) * mm, "radius": 5.5 * mm, "construction": true});
            skPoint(sketch, "E10.4.0.33", {"position": v(46.63, -11.8) * mm});
            skLineSegment(sketch, "E10.4.0.34", {"start": v(9.04, -19.87) * mm, "end": v(19.66, -25.9) * mm});
            skLineSegment(sketch, "E10.4.0.35", {"start": v(54.57, -3.55) * mm, "end": v(57.74, -9.05) * mm});
            skLineSegment(sketch, "E10.4.0.36", {"start": v(33.4, -14.78) * mm, "end": v(36.59, -20.28) * mm});
            skLineSegment(sketch, "E10.4.0.37", {"start": v(16.48, -20.4) * mm, "end": v(22.83, -20.4) * mm});
            skLineSegment(sketch, "E10.4.0.38", {"start": v(65.15, -8.94) * mm, "end": v(58.8, -8.94) * mm});
            skLineSegment(sketch, "E10.4.0.39", {"start": v(22.83, -31.4) * mm, "end": v(16.48, -31.4) * mm});
            skLineSegment(sketch, "E10.4.0.40", {"start": v(36.55, -8.6) * mm, "end": v(33.4, -14.11) * mm});
            skLineSegment(sketch, "E10.4.0.41", {"start": v(48.14, 8.08) * mm, "end": v(54.5, 8.12) * mm});
            skLineSegment(sketch, "E10.4.0.42", {"start": v(22.83, -19.73) * mm, "end": v(16.48, -19.77) * mm});
            skLineSegment(sketch, "E10.4.0.43", {"start": v(45, 2.55) * mm, "end": v(48.14, 8.08) * mm});
            skLineSegment(sketch, "E10.4.0.44", {"start": v(13.3, -25.9) * mm, "end": v(16.48, -20.4) * mm});
            skLineSegment(sketch, "E10.4.0.45", {"start": v(15.4, -19.83) * mm, "end": v(12.25, -25.35) * mm});
            skLineSegment(sketch, "E10.4.0.46", {"start": v(15.43, -31.52) * mm, "end": v(12.26, -37.02) * mm});
            skLineSegment(sketch, "E10.4.0.47", {"start": v(57.74, -9.05) * mm, "end": v(54.57, -14.55) * mm});
            skLineSegment(sketch, "E10.4.0.48", {"start": v(58.8, -8.94) * mm, "end": v(55.62, -3.44) * mm});
            skLineSegment(sketch, "E10.4.0.49", {"start": v(33.41, -25.78) * mm, "end": v(27.06, -25.79) * mm});
            skLineSegment(sketch, "E10.4.0.50", {"start": v(22.83, -20.4) * mm, "end": v(26, -25.9) * mm});
            skLineSegment(sketch, "E10.4.0.51", {"start": v(33.4, -14.11) * mm, "end": v(27.06, -14.16) * mm});
            skLineSegment(sketch, "E10.4.0.52", {"start": v(12.25, -25.35) * mm, "end": v(5.9, -25.39) * mm});
            skLineSegment(sketch, "E10.4.0.53", {"start": v(4.81, -25.44) * mm, "end": v(1.67, -30.96) * mm});
            skLineSegment(sketch, "E10.4.0.54", {"start": v(65.14, 2.06) * mm, "end": v(68.32, -3.43) * mm});
            skLineSegment(sketch, "E10.4.0.55", {"start": v(45.04, -9.05) * mm, "end": v(48.21, -3.55) * mm});
            skLineSegment(sketch, "E10.4.0.56", {"start": v(37.64, -9.17) * mm, "end": v(43.99, -9.17) * mm});
            skLineSegment(sketch, "E10.4.0.57", {"start": v(27.06, -25.79) * mm, "end": v(23.88, -20.29) * mm});
            skLineSegment(sketch, "E10.4.0.58", {"start": v(48.22, -14.55) * mm, "end": v(45.04, -9.05) * mm});
            skLineSegment(sketch, "E10.4.0.59", {"start": v(27.06, -14.16) * mm, "end": v(23.85, -8.68) * mm});
            skLineSegment(sketch, "E10.4.0.60", {"start": v(23.88, -20.29) * mm, "end": v(27.06, -14.79) * mm});
            skLineSegment(sketch, "E10.4.0.61", {"start": v(5.9, -26.02) * mm, "end": v(12.25, -26.02) * mm});
            skLineSegment(sketch, "E10.4.0.62", {"start": v(47.16, -14.67) * mm, "end": v(43.99, -20.17) * mm});
            skLineSegment(sketch, "E10.4.0.63", {"start": v(16.4, -8.77) * mm, "end": v(22.76, -8.73) * mm});
            skLineSegment(sketch, "E10.4.0.64", {"start": v(34.42, -3.06) * mm, "end": v(37.56, 2.46) * mm});
            skLineSegment(sketch, "E10.4.0.65", {"start": v(55.62, -3.44) * mm, "end": v(58.8, 2.06) * mm});
            skLineSegment(sketch, "E10.4.0.66", {"start": v(2.73, -31.52) * mm, "end": v(5.9, -26.02) * mm});
            skLineSegment(sketch, "E10.4.0.67", {"start": v(54.5, 8.12) * mm, "end": v(57.7, 2.64) * mm});
            skLineSegment(sketch, "E10.4.0.68", {"start": v(13.27, -14.3) * mm, "end": v(16.4, -8.77) * mm});
            skLineSegment(sketch, "E10.4.0.69", {"start": v(5.9, -25.39) * mm, "end": v(2.69, -19.91) * mm});
            skLineSegment(sketch, "E10.4.0.70", {"start": v(33.33, -3.11) * mm, "end": v(36.55, -8.6) * mm});
            skLineSegment(sketch, "E10.4.0.71", {"start": v(26, -25.9) * mm, "end": v(22.83, -31.4) * mm});
            skLineSegment(sketch, "E10.4.0.72", {"start": v(5.9, -37.02) * mm, "end": v(2.73, -31.52) * mm});
            skLineSegment(sketch, "E10.4.0.73", {"start": v(34.46, -14.67) * mm, "end": v(37.64, -9.17) * mm});
            skLineSegment(sketch, "E10.4.0.74", {"start": v(48.21, -3.55) * mm, "end": v(54.57, -3.55) * mm});
            skLineSegment(sketch, "E10.4.0.75", {"start": v(43.99, -8.5) * mm, "end": v(37.64, -8.54) * mm});
            skLineSegment(sketch, "E10.4.0.76", {"start": v(5.83, -14.39) * mm, "end": v(12.18, -14.35) * mm});
            skLineSegment(sketch, "E10.4.0.77", {"start": v(2.69, -19.91) * mm, "end": v(5.83, -14.39) * mm});
            skLineSegment(sketch, "E10.4.0.78", {"start": v(37.56, 2.46) * mm, "end": v(43.91, 2.5) * mm});
            skLineSegment(sketch, "E10.4.0.79", {"start": v(25.97, -14.2) * mm, "end": v(22.83, -19.73) * mm});
            skLineSegment(sketch, "E10.4.0.80", {"start": v(-7.89, -25.53) * mm, "end": v(-4.75, -20) * mm});
            skLineSegment(sketch, "E10.4.0.81", {"start": v(48.21, -2.92) * mm, "end": v(45, 2.55) * mm});
            skLineSegment(sketch, "E10.4.0.82", {"start": v(1.6, -19.96) * mm, "end": v(4.81, -25.44) * mm});
            skLineSegment(sketch, "E10.4.0.83", {"start": v(22.76, -8.73) * mm, "end": v(25.97, -14.2) * mm});
            skLineSegment(sketch, "E10.4.0.84", {"start": v(27.06, -14.79) * mm, "end": v(33.4, -14.78) * mm});
            skLineSegment(sketch, "E10.4.0.85", {"start": v(23.85, -8.68) * mm, "end": v(26.98, -3.16) * mm});
            skLineSegment(sketch, "E10.4.0.86", {"start": v(43.99, -20.17) * mm, "end": v(37.64, -20.17) * mm});
            skLineSegment(sketch, "E10.4.0.87", {"start": v(37.64, -20.17) * mm, "end": v(34.46, -14.67) * mm});
            skLineSegment(sketch, "E10.4.0.88", {"start": v(54.57, -14.55) * mm, "end": v(48.22, -14.55) * mm});
            skLineSegment(sketch, "E10.4.0.89", {"start": v(36.59, -20.28) * mm, "end": v(33.41, -25.78) * mm});
            skLineSegment(sketch, "E10.4.0.90", {"start": v(68.32, -3.43) * mm, "end": v(65.15, -8.94) * mm});
            skLineSegment(sketch, "E10.4.0.91", {"start": v(-4.75, -20) * mm, "end": v(1.6, -19.96) * mm});
            skLineSegment(sketch, "E10.4.0.92", {"start": v(47.13, -2.98) * mm, "end": v(43.99, -8.5) * mm});
            skLineSegment(sketch, "E10.4.0.93", {"start": v(57.7, 2.64) * mm, "end": v(54.57, -2.88) * mm});
            skLineSegment(sketch, "E10.4.0.94", {"start": v(1.67, -30.96) * mm, "end": v(-4.68, -31) * mm});
            skLineSegment(sketch, "E10.4.0.95", {"start": v(43.99, -9.17) * mm, "end": v(47.16, -14.67) * mm});
            skLineSegment(sketch, "E10.4.0.96", {"start": v(12.25, -26.02) * mm, "end": v(15.43, -31.52) * mm});
            skLineSegment(sketch, "E10.4.0.97", {"start": v(-4.68, -31) * mm, "end": v(-7.89, -25.53) * mm});
            skLineSegment(sketch, "E10.4.0.98", {"start": v(16.48, -19.77) * mm, "end": v(13.27, -14.3) * mm});
            skLineSegment(sketch, "E10.4.0.99", {"start": v(16.48, -31.4) * mm, "end": v(13.3, -25.9) * mm});
            skLineSegment(sketch, "E10.4.0.100", {"start": v(54.57, -2.88) * mm, "end": v(48.21, -2.92) * mm});
            skLineSegment(sketch, "E10.4.0.101", {"start": v(12.26, -37.02) * mm, "end": v(5.9, -37.02) * mm});
            skLineSegment(sketch, "E10.4.0.102", {"start": v(58.8, 2.06) * mm, "end": v(65.14, 2.06) * mm});
            skLineSegment(sketch, "E10.5.0.0", {"start": v(17.17, -42.67) * mm, "end": v(27.75, -37.05) * mm, "construction": true});
            skPoint(sketch, "E10.5.0.1", {"position": v(67.4, -17.4) * mm});
            skPoint(sketch, "E10.5.0.2", {"position": v(46.24, -28.63) * mm});
            skLineSegment(sketch, "E10.5.0.3", {"start": v(34.02, -26) * mm, "end": v(37.23, -31.49) * mm});
            skCircle(sketch, "E10.5.0.4", {"center": v(62.66, -26.33) * mm, "radius": 5.5 * mm, "construction": true});
            skPoint(sketch, "E10.5.0.5", {"position": v(56.82, -23.02) * mm});
            skLineSegment(sketch, "E10.5.0.6", {"start": v(48.83, -14.82) * mm, "end": v(55.18, -14.78) * mm});
            skLineSegment(sketch, "E10.5.0.7", {"start": v(62.62, -14.68) * mm, "end": v(73.23, -20.71) * mm});
            skLineSegment(sketch, "E10.5.0.8", {"start": v(73.2, -9.06) * mm, "end": v(83.81, -15.1) * mm});
            skLineSegment(sketch, "E10.5.0.9", {"start": v(20.3, -37.15) * mm, "end": v(30.92, -43.18) * mm});
            skCircle(sketch, "E10.5.0.10", {"center": v(30.92, -43.18) * mm, "radius": 5.5 * mm, "construction": true});
            skCircle(sketch, "E10.5.0.11", {"center": v(62.62, -14.68) * mm, "radius": 5.5 * mm, "construction": true});
            skLineSegment(sketch, "E10.5.0.12", {"start": v(59.48, -20.2) * mm, "end": v(56.27, -14.72) * mm});
            skPoint(sketch, "E10.5.0.13", {"position": v(35.67, -34.25) * mm});
            skCircle(sketch, "E10.5.0.14", {"center": v(83.81, -15.1) * mm, "radius": 5.5 * mm, "construction": true});
            skLineSegment(sketch, "E10.5.0.15", {"start": v(41.46, -25.91) * mm, "end": v(52.08, -31.95) * mm});
            skPoint(sketch, "E10.5.0.16", {"position": v(26.16, -45.93) * mm});
            skPoint(sketch, "E10.5.0.17", {"position": v(57.9, -29.08) * mm});
            skCircle(sketch, "E10.5.0.18", {"center": v(73.2, -9.06) * mm, "radius": 5.5 * mm, "construction": true});
            skPoint(sketch, "E10.5.0.19", {"position": v(25.09, -39.86) * mm});
            skCircle(sketch, "E10.5.0.20", {"center": v(52.04, -20.3) * mm, "radius": 5.5 * mm, "construction": true});
            skCircle(sketch, "E10.5.0.21", {"center": v(41.5, -37.56) * mm, "radius": 5.5 * mm, "construction": true});
            skLineSegment(sketch, "E10.5.0.22", {"start": v(52.04, -20.3) * mm, "end": v(62.66, -26.33) * mm});
            skCircle(sketch, "E10.5.0.23", {"center": v(73.23, -20.71) * mm, "radius": 5.5 * mm, "construction": true});
            skCircle(sketch, "E10.5.0.24", {"center": v(52.08, -31.95) * mm, "radius": 5.5 * mm, "construction": true});
            skPoint(sketch, "E10.5.0.25", {"position": v(47.32, -34.7) * mm});
            skPoint(sketch, "E10.5.0.26", {"position": v(79.05, -17.85) * mm});
            skPoint(sketch, "E10.5.0.27", {"position": v(36.74, -40.32) * mm});
            skLineSegment(sketch, "E10.5.0.28", {"start": v(65.76, -9.16) * mm, "end": v(68.97, -14.64) * mm});
            skCircle(sketch, "E10.5.0.29", {"center": v(41.46, -25.91) * mm, "radius": 5.5 * mm, "construction": true});
            skPoint(sketch, "E10.5.0.30", {"position": v(77.98, -11.78) * mm});
            skCircle(sketch, "E10.5.0.31", {"center": v(30.88, -31.53) * mm, "radius": 5.5 * mm, "construction": true});
            skCircle(sketch, "E10.5.0.32", {"center": v(20.3, -37.15) * mm, "radius": 5.5 * mm, "construction": true});
            skPoint(sketch, "E10.5.0.33", {"position": v(68.47, -23.47) * mm});
            skLineSegment(sketch, "E10.5.0.34", {"start": v(30.88, -31.53) * mm, "end": v(41.5, -37.56) * mm});
            skLineSegment(sketch, "E10.5.0.35", {"start": v(76.4, -15.21) * mm, "end": v(79.59, -20.71) * mm});
            skLineSegment(sketch, "E10.5.0.36", {"start": v(55.25, -26.45) * mm, "end": v(58.43, -31.95) * mm});
            skLineSegment(sketch, "E10.5.0.37", {"start": v(38.32, -32.06) * mm, "end": v(44.67, -32.06) * mm});
            skLineSegment(sketch, "E10.5.0.38", {"start": v(86.99, -20.6) * mm, "end": v(80.64, -20.6) * mm});
            skLineSegment(sketch, "E10.5.0.39", {"start": v(44.68, -43.06) * mm, "end": v(38.33, -43.06) * mm});
            skLineSegment(sketch, "E10.5.0.40", {"start": v(58.4, -20.25) * mm, "end": v(55.25, -25.78) * mm});
            skLineSegment(sketch, "E10.5.0.41", {"start": v(69.98, -3.59) * mm, "end": v(76.33, -3.54) * mm});
            skLineSegment(sketch, "E10.5.0.42", {"start": v(44.67, -31.4) * mm, "end": v(38.32, -31.44) * mm});
            skLineSegment(sketch, "E10.5.0.43", {"start": v(66.85, -9.1) * mm, "end": v(69.98, -3.59) * mm});
            skLineSegment(sketch, "E10.5.0.44", {"start": v(35.15, -37.57) * mm, "end": v(38.32, -32.06) * mm});
            skLineSegment(sketch, "E10.5.0.45", {"start": v(37.23, -31.49) * mm, "end": v(34.1, -37) * mm});
            skLineSegment(sketch, "E10.5.0.46", {"start": v(37.27, -43.18) * mm, "end": v(34.1, -48.68) * mm});
            skLineSegment(sketch, "E10.5.0.47", {"start": v(79.59, -20.71) * mm, "end": v(76.41, -26.21) * mm});
            skLineSegment(sketch, "E10.5.0.48", {"start": v(80.64, -20.6) * mm, "end": v(77.46, -15.1) * mm});
            skLineSegment(sketch, "E10.5.0.49", {"start": v(55.25, -37.45) * mm, "end": v(48.9, -37.45) * mm});
            skLineSegment(sketch, "E10.5.0.50", {"start": v(44.67, -32.06) * mm, "end": v(47.85, -37.56) * mm});
            skLineSegment(sketch, "E10.5.0.51", {"start": v(55.25, -25.78) * mm, "end": v(48.9, -25.82) * mm});
            skLineSegment(sketch, "E10.5.0.52", {"start": v(34.1, -37) * mm, "end": v(27.75, -37.05) * mm});
            skLineSegment(sketch, "E10.5.0.53", {"start": v(26.66, -37.1) * mm, "end": v(23.52, -42.63) * mm});
            skLineSegment(sketch, "E10.5.0.54", {"start": v(86.99, -9.6) * mm, "end": v(90.16, -15.1) * mm});
            skLineSegment(sketch, "E10.5.0.55", {"start": v(66.88, -20.72) * mm, "end": v(70.06, -15.22) * mm});
            skLineSegment(sketch, "E10.5.0.56", {"start": v(59.48, -20.83) * mm, "end": v(65.83, -20.83) * mm});
            skLineSegment(sketch, "E10.5.0.57", {"start": v(48.9, -37.45) * mm, "end": v(45.73, -31.95) * mm});
            skLineSegment(sketch, "E10.5.0.58", {"start": v(70.06, -26.22) * mm, "end": v(66.88, -20.72) * mm});
            skLineSegment(sketch, "E10.5.0.59", {"start": v(48.9, -25.82) * mm, "end": v(45.69, -20.34) * mm});
            skLineSegment(sketch, "E10.5.0.60", {"start": v(45.73, -31.95) * mm, "end": v(48.9, -26.45) * mm});
            skLineSegment(sketch, "E10.5.0.61", {"start": v(27.75, -37.68) * mm, "end": v(34.1, -37.68) * mm});
            skLineSegment(sketch, "E10.5.0.62", {"start": v(69, -26.33) * mm, "end": v(65.83, -31.83) * mm});
            skLineSegment(sketch, "E10.5.0.63", {"start": v(38.25, -20.44) * mm, "end": v(44.6, -20.4) * mm});
            skLineSegment(sketch, "E10.5.0.64", {"start": v(56.27, -14.72) * mm, "end": v(59.4, -9.2) * mm});
            skLineSegment(sketch, "E10.5.0.65", {"start": v(77.46, -15.1) * mm, "end": v(80.64, -9.6) * mm});
            skLineSegment(sketch, "E10.5.0.66", {"start": v(24.57, -43.18) * mm, "end": v(27.75, -37.68) * mm});
            skLineSegment(sketch, "E10.5.0.67", {"start": v(76.33, -3.54) * mm, "end": v(79.55, -9.02) * mm});
            skLineSegment(sketch, "E10.5.0.68", {"start": v(35.11, -25.96) * mm, "end": v(38.25, -20.44) * mm});
            skLineSegment(sketch, "E10.5.0.69", {"start": v(27.75, -37.05) * mm, "end": v(24.53, -31.57) * mm});
            skLineSegment(sketch, "E10.5.0.70", {"start": v(55.18, -14.78) * mm, "end": v(58.4, -20.25) * mm});
            skLineSegment(sketch, "E10.5.0.71", {"start": v(47.85, -37.56) * mm, "end": v(44.68, -43.06) * mm});
            skLineSegment(sketch, "E10.5.0.72", {"start": v(27.75, -48.68) * mm, "end": v(24.57, -43.18) * mm});
            skLineSegment(sketch, "E10.5.0.73", {"start": v(56.3, -26.33) * mm, "end": v(59.48, -20.83) * mm});
            skLineSegment(sketch, "E10.5.0.74", {"start": v(70.06, -15.22) * mm, "end": v(76.4, -15.21) * mm});
            skLineSegment(sketch, "E10.5.0.75", {"start": v(65.83, -20.16) * mm, "end": v(59.48, -20.2) * mm});
            skLineSegment(sketch, "E10.5.0.76", {"start": v(27.67, -26.05) * mm, "end": v(34.02, -26) * mm});
            skLineSegment(sketch, "E10.5.0.77", {"start": v(24.53, -31.57) * mm, "end": v(27.67, -26.05) * mm});
            skLineSegment(sketch, "E10.5.0.78", {"start": v(59.4, -9.2) * mm, "end": v(65.76, -9.16) * mm});
            skLineSegment(sketch, "E10.5.0.79", {"start": v(47.81, -25.87) * mm, "end": v(44.67, -31.4) * mm});
            skLineSegment(sketch, "E10.5.0.80", {"start": v(13.95, -37.2) * mm, "end": v(17.1, -31.67) * mm});
            skLineSegment(sketch, "E10.5.0.81", {"start": v(70.06, -14.59) * mm, "end": v(66.85, -9.1) * mm});
            skLineSegment(sketch, "E10.5.0.82", {"start": v(23.44, -31.63) * mm, "end": v(26.66, -37.1) * mm});
            skLineSegment(sketch, "E10.5.0.83", {"start": v(44.6, -20.4) * mm, "end": v(47.81, -25.87) * mm});
            skLineSegment(sketch, "E10.5.0.84", {"start": v(48.9, -26.45) * mm, "end": v(55.25, -26.45) * mm});
            skLineSegment(sketch, "E10.5.0.85", {"start": v(45.69, -20.34) * mm, "end": v(48.83, -14.82) * mm});
            skLineSegment(sketch, "E10.5.0.86", {"start": v(65.83, -31.83) * mm, "end": v(59.48, -31.83) * mm});
            skLineSegment(sketch, "E10.5.0.87", {"start": v(59.48, -31.83) * mm, "end": v(56.3, -26.33) * mm});
            skLineSegment(sketch, "E10.5.0.88", {"start": v(76.41, -26.21) * mm, "end": v(70.06, -26.22) * mm});
            skLineSegment(sketch, "E10.5.0.89", {"start": v(58.43, -31.95) * mm, "end": v(55.25, -37.45) * mm});
            skLineSegment(sketch, "E10.5.0.90", {"start": v(90.16, -15.1) * mm, "end": v(86.99, -20.6) * mm});
            skLineSegment(sketch, "E10.5.0.91", {"start": v(17.1, -31.67) * mm, "end": v(23.44, -31.63) * mm});
            skLineSegment(sketch, "E10.5.0.92", {"start": v(68.97, -14.64) * mm, "end": v(65.83, -20.16) * mm});
            skLineSegment(sketch, "E10.5.0.93", {"start": v(79.55, -9.02) * mm, "end": v(76.4, -14.54) * mm});
            skLineSegment(sketch, "E10.5.0.94", {"start": v(23.52, -42.63) * mm, "end": v(17.17, -42.67) * mm});
            skLineSegment(sketch, "E10.5.0.95", {"start": v(65.83, -20.83) * mm, "end": v(69, -26.33) * mm});
            skLineSegment(sketch, "E10.5.0.96", {"start": v(34.1, -37.68) * mm, "end": v(37.27, -43.18) * mm});
            skLineSegment(sketch, "E10.5.0.97", {"start": v(17.17, -42.67) * mm, "end": v(13.95, -37.2) * mm});
            skLineSegment(sketch, "E10.5.0.98", {"start": v(38.32, -31.44) * mm, "end": v(35.11, -25.96) * mm});
            skLineSegment(sketch, "E10.5.0.99", {"start": v(38.33, -43.06) * mm, "end": v(35.15, -37.57) * mm});
            skLineSegment(sketch, "E10.5.0.100", {"start": v(76.4, -14.54) * mm, "end": v(70.06, -14.59) * mm});
            skLineSegment(sketch, "E10.5.0.101", {"start": v(34.1, -48.68) * mm, "end": v(27.75, -48.68) * mm});
            skLineSegment(sketch, "E10.5.0.102", {"start": v(80.64, -9.6) * mm, "end": v(86.99, -9.6) * mm});
            skLineSegment(sketch, "E10.direction1", {"start": v(-92.05, 15.64) * mm, "end": v(-70.2, 3.98) * mm, "construction": true});
            skSolve(sketch);
        }
        {
            var Q0;
            Q0=makeQuery(id+"F3.imprint","IMPRINT",FACE,{"disambiguationData":[TD([[makeQuery(id+"F3.imprint","IMPRINT",EDGE,{"derivedFrom":sQuery(id+"F3.wireOp",EDGE,"E10.1.0.41")}),-1.0]])]});
            var Q1;
            Q1=makeQuery(id+"F3.imprint","IMPRINT",FACE,{"disambiguationData":[TD([[makeQuery(id+"F3.imprint","IMPRINT",EDGE,{"derivedFrom":sQuery(id+"F3.wireOp",EDGE,"E10.4.0.12")}),-1.0]])]});
            var Q2;
            Q2=makeQuery(id+"F3.imprint","IMPRINT",FACE,{"disambiguationData":[TD([[makeQuery(id+"F3.imprint","IMPRINT",EDGE,{"derivedFrom":sQuery(id+"F3.wireOp",EDGE,"E10.5.0.6")}),-1.0]])]});
            var Q3;
            Q3=makeQuery(id+"F3.imprint","IMPRINT",FACE,{"disambiguationData":[TD([[makeQuery(id+"F3.imprint","IMPRINT",EDGE,{"derivedFrom":sQuery(id+"F3.wireOp",EDGE,"E10.5.0.12")}),-1.0]])]});
            var Q4;
            {var subQ0=sQuery(id+"F3.wireOp",EDGE,"E10.1.0.42");Q4=makeQuery(id+"F3.imprint","IMPRINT",FACE,{"disambiguationData":[TD([[makeQuery(id+"F3.imprint","IMPRINT",EDGE,{"derivedFrom":subQ0}),-1.0]])]});}
            var Q5;
            Q5=makeQuery(id+"F3.imprint","IMPRINT",FACE,{"disambiguationData":[TD([[makeQuery(id+"F3.imprint","IMPRINT",EDGE,{"derivedFrom":sQuery(id+"F3.wireOp",EDGE,"E10.5.0.80")}),-1.0]])]});
            var Q6;
            Q6=makeQuery(id+"F3.imprint","IMPRINT",FACE,{"disambiguationData":[TD([[makeQuery(id+"F3.imprint","IMPRINT",EDGE,{"derivedFrom":sQuery(id+"F3.wireOp",EDGE,"E10.3.0.41")}),-1.0]])]});
            var Q7;
            Q7=makeQuery(id+"F3.imprint","IMPRINT",FACE,{"disambiguationData":[TD([[makeQuery(id+"F3.imprint","IMPRINT",EDGE,{"derivedFrom":sQuery(id+"F3.wireOp",EDGE,"E10.4.0.6")}),-1.0]])]});
            var Q8;
            {var subQ3=sQuery(id+"F3.wireOp",EDGE,"E10.5.0.3");Q8=makeQuery(id+"F3.imprint","IMPRINT",FACE,{"disambiguationData":[TD([[makeQuery(id+"F3.imprint","IMPRINT",EDGE,{"derivedFrom":subQ3}),-1.0]])]});}
            var Q9;
            {var subQ3=sQuery(id+"F3.wireOp",EDGE,"E10.4.0.3");Q9=makeQuery(id+"F3.imprint","IMPRINT",FACE,{"disambiguationData":[TD([[makeQuery(id+"F3.imprint","IMPRINT",EDGE,{"derivedFrom":subQ3}),-1.0]])]});}
            var Q10;
            {var subQ0=sQuery(id+"F3.wireOp",EDGE,"E10.5.0.42");Q10=makeQuery(id+"F3.imprint","IMPRINT",FACE,{"disambiguationData":[TD([[makeQuery(id+"F3.imprint","IMPRINT",EDGE,{"derivedFrom":subQ0}),-1.0]])]});}
            var Q11;
            Q11=makeQuery(id+"F3.imprint","IMPRINT",FACE,{"disambiguationData":[TD([[makeQuery(id+"F3.imprint","IMPRINT",EDGE,{"derivedFrom":sQuery(id+"F3.wireOp",EDGE,"E10.4.0.80")}),-1.0]])]});
            var Q12;
            Q12=makeQuery(id+"F3.imprint","IMPRINT",FACE,{"disambiguationData":[TD([[makeQuery(id+"F3.imprint","IMPRINT",EDGE,{"derivedFrom":sQuery(id+"F3.wireOp",EDGE,"E10.2.0.41")}),-1.0]])]});
            var Q13;
            Q13=makeQuery(id+"F3.imprint","IMPRINT",FACE,{"disambiguationData":[TD([[makeQuery(id+"F3.imprint","IMPRINT",EDGE,{"derivedFrom":sQuery(id+"F3.wireOp",EDGE,"E10.2.0.6")}),-1.0]])]});
            var Q14;
            Q14=makeQuery(id+"F3.imprint","IMPRINT",FACE,{"disambiguationData":[TD([[makeQuery(id+"F3.imprint","IMPRINT",EDGE,{"derivedFrom":sQuery(id+"F3.wireOp",EDGE,"E10.2.0.80")}),-1.0]])]});
            var Q15;
            {var subQ1=sQuery(id+"F3.wireOp",EDGE,"E9.4.0.1");Q15=makeQuery(id+"F3.imprint","IMPRINT",FACE,{"disambiguationData":[TD([[makeQuery(id+"F3.imprint","IMPRINT",EDGE,{"derivedFrom":subQ1}),-1.0]])]});}
            var Q16;
            Q16=makeQuery(id+"F3.imprint","IMPRINT",FACE,{"disambiguationData":[TD([[makeQuery(id+"F3.imprint","IMPRINT",EDGE,{"derivedFrom":sQuery(id+"F3.wireOp",EDGE,"E10.1.0.12")}),-1.0]])]});
            var Q17;
            {var subQ0=sQuery(id+"F3.wireOp",EDGE,"E10.2.0.42");Q17=makeQuery(id+"F3.imprint","IMPRINT",FACE,{"disambiguationData":[TD([[makeQuery(id+"F3.imprint","IMPRINT",EDGE,{"derivedFrom":subQ0}),-1.0]])]});}
            var Q18;
            {var subQ3=sQuery(id+"F3.wireOp",EDGE,"E10.2.0.3");Q18=makeQuery(id+"F3.imprint","IMPRINT",FACE,{"disambiguationData":[TD([[makeQuery(id+"F3.imprint","IMPRINT",EDGE,{"derivedFrom":subQ3}),-1.0]])]});}
            var Q19;
            {var subQ0=sQuery(id+"F3.wireOp",EDGE,"E10.4.0.42");Q19=makeQuery(id+"F3.imprint","IMPRINT",FACE,{"disambiguationData":[TD([[makeQuery(id+"F3.imprint","IMPRINT",EDGE,{"derivedFrom":subQ0}),-1.0]])]});}
            var Q20;
            Q20=makeQuery(id+"F3.imprint","IMPRINT",FACE,{"disambiguationData":[TD([[makeQuery(id+"F3.imprint","IMPRINT",EDGE,{"derivedFrom":sQuery(id+"F3.wireOp",EDGE,"E10.3.0.12")}),-1.0]])]});
            var Q21;
            {var subQ1=sQuery(id+"F3.wireOp",EDGE,"E9.5.0.1");Q21=makeQuery(id+"F3.imprint","IMPRINT",FACE,{"disambiguationData":[TD([[makeQuery(id+"F3.imprint","IMPRINT",EDGE,{"derivedFrom":subQ1}),-1.0]])]});}
            var Q22;
            Q22=makeQuery(id+"F3.imprint","IMPRINT",FACE,{"disambiguationData":[TD([[makeQuery(id+"F3.imprint","IMPRINT",EDGE,{"derivedFrom":sQuery(id+"F3.wireOp",EDGE,"E10.4.0.41")}),-1.0]])]});
            var Q23;
            Q23=makeQuery(id+"F3.imprint","IMPRINT",FACE,{"disambiguationData":[TD([[makeQuery(id+"F3.imprint","IMPRINT",EDGE,{"derivedFrom":sQuery(id+"F3.wireOp",EDGE,"E10.2.0.12")}),-1.0]])]});
            var Q24;
            Q24=makeQuery(id+"F3.imprint","IMPRINT",FACE,{"disambiguationData":[TD([[makeQuery(id+"F3.imprint","IMPRINT",EDGE,{"derivedFrom":sQuery(id+"F3.wireOp",EDGE,"E10.1.0.6")}),-1.0]])]});
            var Q25;
            {var subQ3=sQuery(id+"F3.wireOp",EDGE,"E10.3.0.3");Q25=makeQuery(id+"F3.imprint","IMPRINT",FACE,{"disambiguationData":[TD([[makeQuery(id+"F3.imprint","IMPRINT",EDGE,{"derivedFrom":subQ3}),-1.0]])]});}
            var Q26;
            Q26=makeQuery(id+"F3.imprint","IMPRINT",FACE,{"disambiguationData":[TD([[makeQuery(id+"F3.imprint","IMPRINT",EDGE,{"derivedFrom":sQuery(id+"F3.wireOp",EDGE,"E10.4.0.36")}),-1.0]])]});
            var Q27;
            Q27=makeQuery(id+"F3.imprint","IMPRINT",FACE,{"disambiguationData":[TD([[makeQuery(id+"F3.imprint","IMPRINT",EDGE,{"derivedFrom":sQuery(id+"F3.wireOp",EDGE,"E10.5.0.41")}),-1.0]])]});
            var Q28;
            Q28=makeQuery(id+"F3.imprint","IMPRINT",FACE,{"disambiguationData":[TD([[makeQuery(id+"F3.imprint","IMPRINT",EDGE,{"derivedFrom":sQuery(id+"F3.wireOp",EDGE,"E10.5.0.46")}),-1.0]])]});
            var Q29;
            Q29=makeQuery(id+"F3.imprint","IMPRINT",FACE,{"disambiguationData":[TD([[makeQuery(id+"F3.imprint","IMPRINT",EDGE,{"derivedFrom":sQuery(id+"F3.wireOp",EDGE,"E9.4.0.7")}),-1.0]])]});
            var Q30;
            {var subQ1=sQuery(id+"F3.wireOp",EDGE,"E9.2.0.1");Q30=makeQuery(id+"F3.imprint","IMPRINT",FACE,{"disambiguationData":[TD([[makeQuery(id+"F3.imprint","IMPRINT",EDGE,{"derivedFrom":subQ1}),-1.0]])]});}
            var Q31;
            {var subQ0=sQuery(id+"F3.wireOp",EDGE,"E10.3.0.42");Q31=makeQuery(id+"F3.imprint","IMPRINT",FACE,{"disambiguationData":[TD([[makeQuery(id+"F3.imprint","IMPRINT",EDGE,{"derivedFrom":subQ0}),-1.0]])]});}
            var Q32;
            {var subQ1=sQuery(id+"F3.wireOp",EDGE,"E9.3.0.1");Q32=makeQuery(id+"F3.imprint","IMPRINT",FACE,{"disambiguationData":[TD([[makeQuery(id+"F3.imprint","IMPRINT",EDGE,{"derivedFrom":subQ1}),-1.0]])]});}
            var Q33;
            Q33=makeQuery(id+"F3.imprint","IMPRINT",FACE,{"disambiguationData":[TD([[makeQuery(id+"F3.imprint","IMPRINT",EDGE,{"derivedFrom":sQuery(id+"F3.wireOp",EDGE,"E9.2.0.7")}),-1.0]])]});
            var Q34;
            Q34=makeQuery(id+"F3.imprint","IMPRINT",FACE,{"disambiguationData":[TD([[makeQuery(id+"F3.imprint","IMPRINT",EDGE,{"derivedFrom":sQuery(id+"F3.wireOp",EDGE,"E10.3.0.35")}),-1.0]])]});
            var Q35;
            Q35=makeQuery(id+"F3.imprint","IMPRINT",FACE,{"disambiguationData":[TD([[makeQuery(id+"F3.imprint","IMPRINT",EDGE,{"derivedFrom":sQuery(id+"F3.wireOp",EDGE,"E10.4.0.38")}),-1.0]])]});
            var Q36;
            {var subQ1=sQuery(id+"F3.wireOp",EDGE,"E10.3.0.37");Q36=makeQuery(id+"F3.imprint","IMPRINT",FACE,{"disambiguationData":[TD([[makeQuery(id+"F3.imprint","IMPRINT",EDGE,{"derivedFrom":subQ1}),-1.0]])]});}
            var Q37;
            {var subQ1=sQuery(id+"F3.wireOp",EDGE,"E10.4.0.37");Q37=makeQuery(id+"F3.imprint","IMPRINT",FACE,{"disambiguationData":[TD([[makeQuery(id+"F3.imprint","IMPRINT",EDGE,{"derivedFrom":subQ1}),-1.0]])]});}
            var Q38;
            Q38=makeQuery(id+"F3.imprint","IMPRINT",FACE,{"disambiguationData":[TD([[makeQuery(id+"F3.imprint","IMPRINT",EDGE,{"derivedFrom":sQuery(id+"F3.wireOp",EDGE,"E10.3.0.46")}),-1.0]])]});
            var Q39;
            {var subQ1=sQuery(id+"F3.wireOp",EDGE,"E10.3.0.56");Q39=makeQuery(id+"F3.imprint","IMPRINT",FACE,{"disambiguationData":[TD([[makeQuery(id+"F3.imprint","IMPRINT",EDGE,{"derivedFrom":subQ1}),-1.0]])]});}
            var Q40;
            {var subQ3=sQuery(id+"F3.wireOp",EDGE,"E10.1.0.3");Q40=makeQuery(id+"F3.imprint","IMPRINT",FACE,{"disambiguationData":[TD([[makeQuery(id+"F3.imprint","IMPRINT",EDGE,{"derivedFrom":subQ3}),-1.0]])]});}
            var Q41;
            {var subQ1=sQuery(id+"F3.wireOp",EDGE,"E9.1.0.1");Q41=makeQuery(id+"F3.imprint","IMPRINT",FACE,{"disambiguationData":[TD([[makeQuery(id+"F3.imprint","IMPRINT",EDGE,{"derivedFrom":subQ1}),-1.0]])]});}
            var Q42;
            Q42=makeQuery(id+"F3.imprint","IMPRINT",FACE,{"disambiguationData":[TD([[makeQuery(id+"F3.imprint","IMPRINT",EDGE,{"derivedFrom":sQuery(id+"F3.wireOp",EDGE,"E9.5.0.7")}),-1.0]])]});
            var Q43;
            Q43=makeQuery(id+"F3.imprint","IMPRINT",FACE,{"disambiguationData":[TD([[makeQuery(id+"F3.imprint","IMPRINT",EDGE,{"derivedFrom":sQuery(id+"F3.wireOp",EDGE,"E10.3.0.36")}),-1.0]])]});
            var Q44;
            Q44=makeQuery(id+"F3.imprint","IMPRINT",FACE,{"disambiguationData":[TD([[makeQuery(id+"F3.imprint","IMPRINT",EDGE,{"derivedFrom":sQuery(id+"F3.wireOp",EDGE,"E10.2.0.46")}),-1.0]])]});
            var Q45;
            Q45=makeQuery(id+"F3.imprint","IMPRINT",FACE,{"disambiguationData":[TD([[makeQuery(id+"F3.imprint","IMPRINT",EDGE,{"derivedFrom":sQuery(id+"F3.wireOp",EDGE,"E10.3.0.38")}),-1.0]])]});
            var Q46;
            {var subQ1=sQuery(id+"F3.wireOp",EDGE,"E10.4.0.56");Q46=makeQuery(id+"F3.imprint","IMPRINT",FACE,{"disambiguationData":[TD([[makeQuery(id+"F3.imprint","IMPRINT",EDGE,{"derivedFrom":subQ1}),-1.0]])]});}
            var Q47;
            Q47=makeQuery(id+"F3.imprint","IMPRINT",FACE,{"disambiguationData":[TD([[makeQuery(id+"F3.imprint","IMPRINT",EDGE,{"derivedFrom":sQuery(id+"F3.wireOp",EDGE,"E10.1.0.38")}),-1.0]])]});
            var Q48;
            Q48=makeQuery(id+"F3.imprint","IMPRINT",FACE,{"disambiguationData":[TD([[makeQuery(id+"F3.imprint","IMPRINT",EDGE,{"derivedFrom":sQuery(id+"F3.wireOp",EDGE,"E9.1.0.7")}),-1.0]])]});
            var Q49;
            Q49=makeQuery(id+"F3.imprint","IMPRINT",FACE,{"disambiguationData":[TD([[makeQuery(id+"F3.imprint","IMPRINT",EDGE,{"derivedFrom":sQuery(id+"F3.wireOp",EDGE,"E9.3.0.7")}),-1.0]])]});
            var Q50;
            Q50=makeQuery(id+"F3.imprint","IMPRINT",FACE,{"disambiguationData":[TD([[makeQuery(id+"F3.imprint","IMPRINT",EDGE,{"derivedFrom":sQuery(id+"F3.wireOp",EDGE,"E10.4.0.35")}),-1.0]])]});
            var Q51;
            Q51=makeQuery(id+"F3.imprint","IMPRINT",FACE,{"disambiguationData":[TD([[makeQuery(id+"F3.imprint","IMPRINT",EDGE,{"derivedFrom":sQuery(id+"F3.wireOp",EDGE,"E10.1.0.35")}),-1.0]])]});
            var Q52;
            Q52=makeQuery(id+"F3.imprint","IMPRINT",FACE,{"disambiguationData":[TD([[makeQuery(id+"F3.imprint","IMPRINT",EDGE,{"derivedFrom":sQuery(id+"F3.wireOp",EDGE,"E10.4.0.46")}),-1.0]])]});
            var Q53;
            Q53=makeQuery(id+"F3.imprint","IMPRINT",FACE,{"disambiguationData":[TD([[makeQuery(id+"F3.imprint","IMPRINT",EDGE,{"derivedFrom":sQuery(id+"F3.wireOp",EDGE,"E10.1.0.46")}),-1.0]])]});
            var Q54;
            {var subQ3=sQuery(id+"F3.wireOp",EDGE,"E7.0");Q54=makeQuery(id+"F3.imprint","IMPRINT",FACE,{"disambiguationData":[TD([[makeQuery(id+"F3.imprint","IMPRINT",EDGE,{"derivedFrom":subQ3}),-1.0]])]});}
            var Q55;
            Q55=makeQuery(id+"F3.imprint","IMPRINT",FACE,{"disambiguationData":[TD([[makeQuery(id+"F3.imprint","IMPRINT",EDGE,{"derivedFrom":sQuery(id+"F3.wireOp",EDGE,"E10.1.0.80")}),-1.0]])]});
            var Q56;
            Q56=makeQuery(id+"F3.imprint","IMPRINT",FACE,{"disambiguationData":[TD([[makeQuery(id+"F3.imprint","IMPRINT",EDGE,{"derivedFrom":sQuery(id+"F3.wireOp",EDGE,"E10.5.0.38")}),-1.0]])]});
            var Q57;
            {var subQ0=sQuery(id+"F3.wireOp",EDGE,"E6.1");Q57=makeQuery(id+"F3.imprint","IMPRINT",FACE,{"disambiguationData":[TD([[makeQuery(id+"F3.imprint","IMPRINT",EDGE,{"derivedFrom":subQ0}),-1.0]])]});}
            var Q58;
            Q58=makeQuery(id+"F3.imprint","IMPRINT",FACE,{"disambiguationData":[TD([[makeQuery(id+"F3.imprint","IMPRINT",EDGE,{"derivedFrom":sQuery(id+"F3.wireOp",EDGE,"E10.3.0.80")}),-1.0]])]});
            var Q59;
            Q59=makeQuery(id+"F3.imprint","IMPRINT",FACE,{"disambiguationData":[TD([[makeQuery(id+"F3.imprint","IMPRINT",EDGE,{"derivedFrom":sQuery(id+"F3.wireOp",EDGE,"E10.3.0.6")}),-1.0]])]});
            var Q60;
            Q60=makeQuery(id+"F3.imprint","IMPRINT",FACE,{"disambiguationData":[TD([[makeQuery(id+"F3.imprint","IMPRINT",EDGE,{"derivedFrom":sQuery(id+"F3.wireOp",EDGE,"E10.1.0.36")}),-1.0]])]});
            var Q61;
            {var subQ1=sQuery(id+"F3.wireOp",EDGE,"E10.5.0.56");Q61=makeQuery(id+"F3.imprint","IMPRINT",FACE,{"disambiguationData":[TD([[makeQuery(id+"F3.imprint","IMPRINT",EDGE,{"derivedFrom":subQ1}),-1.0]])]});}
            var Q62;
            {var subQ1=sQuery(id+"F3.wireOp",EDGE,"E10.1.0.56");Q62=makeQuery(id+"F3.imprint","IMPRINT",FACE,{"disambiguationData":[TD([[makeQuery(id+"F3.imprint","IMPRINT",EDGE,{"derivedFrom":subQ1}),-1.0]])]});}
            var Q63;
            {var subQ1=sQuery(id+"F3.wireOp",EDGE,"E10.1.0.37");Q63=makeQuery(id+"F3.imprint","IMPRINT",FACE,{"disambiguationData":[TD([[makeQuery(id+"F3.imprint","IMPRINT",EDGE,{"derivedFrom":subQ1}),-1.0]])]});}
            var Q64;
            {var subQ1=sQuery(id+"F3.wireOp",EDGE,"E10.2.0.37");Q64=makeQuery(id+"F3.imprint","IMPRINT",FACE,{"disambiguationData":[TD([[makeQuery(id+"F3.imprint","IMPRINT",EDGE,{"derivedFrom":subQ1}),-1.0]])]});}
            var Q65;
            Q65=makeQuery(id+"F3.imprint","IMPRINT",FACE,{"disambiguationData":[TD([[makeQuery(id+"F3.imprint","IMPRINT",EDGE,{"derivedFrom":sQuery(id+"F3.wireOp",EDGE,"E10.2.0.38")}),-1.0]])]});
            var Q66;
            Q66=makeQuery(id+"F3.imprint","IMPRINT",FACE,{"disambiguationData":[TD([[makeQuery(id+"F3.imprint","IMPRINT",EDGE,{"derivedFrom":sQuery(id+"F3.wireOp",EDGE,"E10.2.0.35")}),-1.0]])]});
            var Q67;
            Q67=makeQuery(id+"F3.imprint","IMPRINT",FACE,{"disambiguationData":[TD([[makeQuery(id+"F3.imprint","IMPRINT",EDGE,{"derivedFrom":sQuery(id+"F3.wireOp",EDGE,"E10.5.0.36")}),-1.0]])]});
            var Q68;
            {var subQ1=sQuery(id+"F3.wireOp",EDGE,"E10.2.0.56");Q68=makeQuery(id+"F3.imprint","IMPRINT",FACE,{"disambiguationData":[TD([[makeQuery(id+"F3.imprint","IMPRINT",EDGE,{"derivedFrom":subQ1}),-1.0]])]});}
            var Q69;
            Q69=makeQuery(id+"F3.imprint","IMPRINT",FACE,{"disambiguationData":[TD([[makeQuery(id+"F3.imprint","IMPRINT",EDGE,{"derivedFrom":sQuery(id+"F3.wireOp",EDGE,"E10.2.0.36")}),-1.0]])]});
            var Q70;
            Q70=makeQuery(id+"F3.imprint","IMPRINT",FACE,{"disambiguationData":[TD([[makeQuery(id+"F3.imprint","IMPRINT",EDGE,{"derivedFrom":sQuery(id+"F3.wireOp",EDGE,"E10.5.0.35")}),-1.0]])]});
            var Q71;
            {var subQ1=sQuery(id+"F3.wireOp",EDGE,"E10.5.0.37");Q71=makeQuery(id+"F3.imprint","IMPRINT",FACE,{"disambiguationData":[TD([[makeQuery(id+"F3.imprint","IMPRINT",EDGE,{"derivedFrom":subQ1}),-1.0]])]});}
            extrude(context, id + "F4", {"entities" : qUnion([Q0, Q1, Q2, Q3, Q4, Q5, Q6, Q7, Q8, Q9, Q10, Q11, Q12, Q13, Q14, Q15, Q16, Q17, Q18, Q19, Q20, Q21, Q22, Q23, Q24, Q25, Q26, Q27, Q28, Q29, Q30, Q31, Q32, Q33, Q34, Q35, Q36, Q37, Q38, Q39, Q40, Q41, Q42, Q43, Q44, Q45, Q46, Q47, Q48, Q49, Q50, Q51, Q52, Q53, Q54, Q55, Q56, Q57, Q58, Q59, Q60, Q61, Q62, Q63, Q64, Q65, Q66, Q67, Q68, Q69, Q70, Q71]), "operationType" : NewBodyOperationType.REMOVE, "endBound" : BoundingType.THROUGH_ALL, "oppositeDirection" : true, "depth" : 25 * mm, "offsetDistance" : 25 * mm});
        }
        {
            var Q0;
            Q0=makeQuery(id+"F4.boolean.opBoolean","SPLIT",FACE,{"disambiguationData":[TD([makeQuery(id+"F4.opExtrude","SWEPT_FACE",FACE,{"disambiguationData":[OSD([sQuery(id+"F3.wireOp",EDGE,"E10.3.0.66")])]})])],"derivedFrom":makeQuery(id+"F1.opRevolve","SWEPT_FACE",FACE,{"disambiguationData":[OSD([sQuery(id+"F0.wireOp",EDGE,"E5")])]})});
            var sketch = newSketch(context, id + "F5", { "sketchPlane" : qUnion([Q0])});
            skCircle(sketch, "E11", {"center": v(-21.4, -91.3) * mm, "radius": 24.14 * mm});
            skPoint(sketch, "E11.first.point", {"position": v(-21, -115.44) * mm});
            skPoint(sketch, "E11.second.point", {"position": v(-18.96, -67.29) * mm});
            skPoint(sketch, "E11.third.point", {"position": v(-45.29, -87.79) * mm});
            skSolve(sketch);
        }
        {
            var Q0;
            Q0=makeQuery(id+"F5.imprint","IMPRINT",FACE,{"disambiguationData":[TD([[makeQuery(id+"F5.imprint","IMPRINT",EDGE,{"disambiguationData":[OD(0.0)],"derivedFrom":sQuery(id+"F5.wireOp",EDGE,"E11")}),-1.0]])]});
            var Q1;
            Q1=makeQuery(id+"F5.imprint","IMPRINT",FACE,{"disambiguationData":[TD([[makeQuery(id+"F5.imprint","IMPRINT",EDGE,{"disambiguationData":[OD(1.0)],"derivedFrom":sQuery(id+"F5.wireOp",EDGE,"E11")}),1.0]])]});
            extrude(context, id + "F6", {"entities" : qUnion([Q0, Q1]), "oppositeDirection" : true, "depth" : 5 * mm, "offsetDistance" : 25 * mm});
        }
    });
